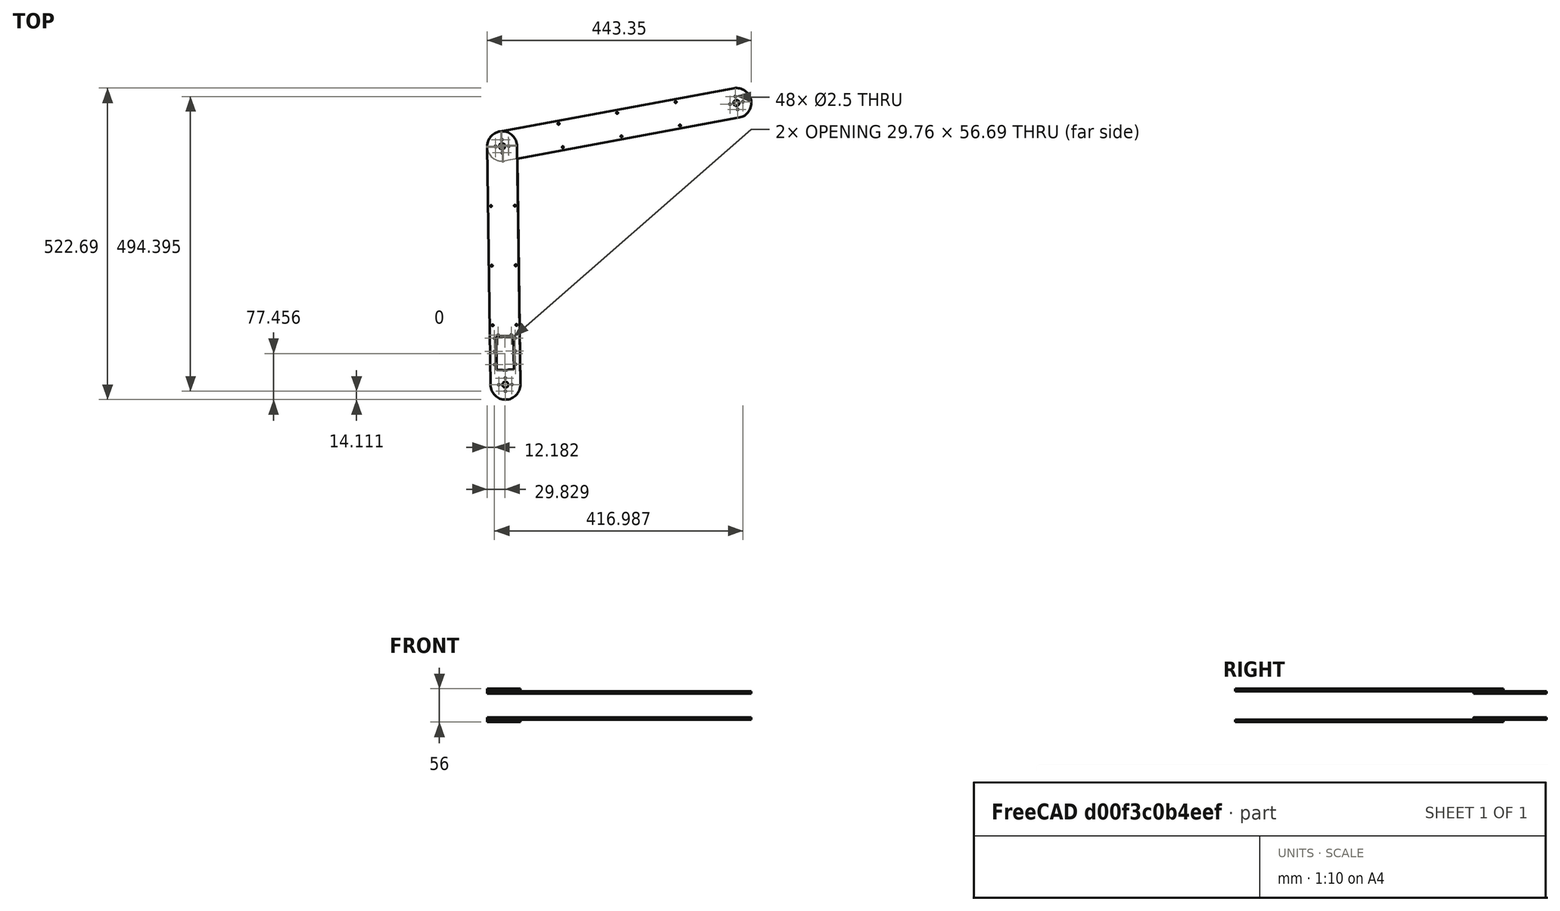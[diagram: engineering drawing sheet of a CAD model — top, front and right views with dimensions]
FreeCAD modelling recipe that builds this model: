
FCSTD DOCUMENT  (FreeCAD 1.0R39109 (Git))
Label: arm_assembly_def
License: All rights reserved
LicenseURL: https://en.wikipedia.org/wiki/All_rights_reserved
objects: App::FeaturePython×16, App::Link×10, Sketcher::SketchObject×4, PartDesign::Pad×4, PartDesign::Body×4, Assembly::JointGroup×1, Assembly::AssemblyObject×1
note: 24 computed .brp shape members not serialized (recipe doc carries the construction recipe); baked Part::Feature solids carry a one-line shape summary decoded from their .brp
EXTERNAL_REF file=srv.FCStd obj=Part__Feature
EXTERNAL_REF file=pulleys/gt2_24T_pulley_open.FCStd obj=Body
EXTERNAL_REF file=pulleys/gt2_48T_pulley.FCStd obj=Body
EXTERNAL_REF file=pulleys/gt2_48T_pulley_double.FCStd obj=Body
EXTERNAL_REF file=pulleys/gt2_24T_pulley_open.FCStd obj=Body001

FEATURE [Sketcher::SketchObject] Sketch
  ArcFitTolerance = 1e-06
  AttachmentSupport = -> [XY_Plane]
  FullyConstrained = false
  MakeInternals = false
  MapMode = 5
  sketch-geometry (67):
    g0: LineSegment [constr] StartX=1.5008e-12 StartY=20 StartZ=0 EndX=1.5008e-12 EndY=-20 EndZ=0
    g1: LineSegment [constr] StartX=-2.359e-12 StartY=0 StartZ=0 EndX=-2.359e-12 EndY=400 EndZ=0
    g2: LineSegment [constr] StartX=1.5008e-12 StartY=20 StartZ=0 EndX=1.5008e-12 EndY=25 EndZ=0
    g3: Circle CenterX=-2.359e-12 CenterY=400 CenterZ=0 NormalX=0 NormalY=0 NormalZ=1 AngleXU=0 Radius=5
    g4: Circle CenterX=-2.359e-12 CenterY=400 CenterZ=0 NormalX=0 NormalY=0 NormalZ=1 AngleXU=0 Radius=2
    g5: Circle CenterX=-10.9997 CenterY=400 CenterZ=0 NormalX=0 NormalY=0 NormalZ=1 AngleXU=0 Radius=1.25
    g6: Circle CenterX=0 CenterY=389 CenterZ=0 NormalX=0 NormalY=0 NormalZ=1 AngleXU=0 Radius=1.25
    g7: Circle CenterX=10.9997 CenterY=400 CenterZ=0 NormalX=0 NormalY=0 NormalZ=1 AngleXU=0 Radius=1.25
    g8: Circle CenterX=0 CenterY=411 CenterZ=0 NormalX=0 NormalY=0 NormalZ=1 AngleXU=0 Radius=1.25
    g9: LineSegment [constr] StartX=0 StartY=-5 StartZ=0 EndX=0 EndY=5.99996 EndZ=0
    g10: Circle [constr] CenterX=0 CenterY=0 CenterZ=0 NormalX=0 NormalY=0 NormalZ=1 AngleXU=0 Radius=14
    g11: LineSegment [constr] StartX=0 StartY=0 StartZ=0 EndX=25.23 EndY=0 EndZ=0
    g12: Circle [constr] CenterX=0 CenterY=-3.8e-05 CenterZ=0 NormalX=0 NormalY=0 NormalZ=1 AngleXU=0 Radius=11
    g13: Circle CenterX=0 CenterY=0 CenterZ=0 NormalX=0 NormalY=0 NormalZ=1 AngleXU=0 Radius=5
    g14: Circle CenterX=10.9997 CenterY=0 CenterZ=0 NormalX=0 NormalY=0 NormalZ=1 AngleXU=0 Radius=1.25
    g15: Circle CenterX=-10.9997 CenterY=0 CenterZ=0 NormalX=0 NormalY=0 NormalZ=1 AngleXU=0 Radius=1.25
    g16: Circle CenterX=0 CenterY=-10.9997 CenterZ=0 NormalX=0 NormalY=0 NormalZ=1 AngleXU=0 Radius=1.25
    g17: Circle CenterX=0 CenterY=11 CenterZ=0 NormalX=0 NormalY=0 NormalZ=1 AngleXU=0 Radius=1.25
    g18: LineSegment [constr] StartX=0 StartY=0 StartZ=0 EndX=-25 EndY=0 EndZ=0
    g19: LineSegment [constr] StartX=20.1368 StartY=86.0999 StartZ=0 EndX=20.1368 EndY=24.9999 EndZ=0
    g20: LineSegment [constr] StartX=0.036848 StartY=80.5 StartZ=0 EndX=14.5368 EndY=80.5 EndZ=0
    g21: LineSegment StartX=14.5368 StartY=80.5 StartZ=0 EndX=-14.4632 EndY=80.5 EndZ=0
    g22: LineSegment StartX=14.5368 StartY=80.5 StartZ=0 EndX=14.5368 EndY=24.9999 EndZ=0
    g23: Circle CenterX=11.0368 CenterY=83.3 CenterZ=0 NormalX=0 NormalY=0 NormalZ=1 AngleXU=0 Radius=1.25
    g24: Circle CenterX=17.3368 CenterY=78 CenterZ=0 NormalX=0 NormalY=0 NormalZ=1 AngleXU=0 Radius=1.25
    g25: LineSegment [constr] StartX=-20.0632 StartY=86.0999 StartZ=0 EndX=20.1368 EndY=86.0999 EndZ=0
    g26: Circle CenterX=17.3368 CenterY=56 CenterZ=0 NormalX=0 NormalY=0 NormalZ=1 AngleXU=0 Radius=1.25
    g27: Circle CenterX=17.3368 CenterY=34 CenterZ=0 NormalX=0 NormalY=0 NormalZ=1 AngleXU=0 Radius=1.25
    g28: Circle [constr] CenterX=0.036848 CenterY=37.9999 CenterZ=0 NormalX=0 NormalY=0 NormalZ=1 AngleXU=0 Radius=14
    g29: ArcOfCircle CenterX=0.036848 CenterY=37.9999 CenterZ=0 NormalX=0 NormalY=0 NormalZ=1 AngleXU=0 Radius=14 StartAngle=4.33214 EndAngle=5.09264
    g30: LineSegment StartX=5.233 StartY=24.9999 StartZ=0 EndX=14.5368 EndY=24.9999 EndZ=0
    g31: LineSegment [constr] StartX=14.5368 StartY=24.9999 StartZ=0 EndX=20.1368 EndY=24.9999 EndZ=0
    g32: LineSegment [constr] StartX=17.3368 StartY=56 StartZ=0 EndX=-17.2632 EndY=56 EndZ=0
    g33: LineSegment [constr] StartX=-20.0632 StartY=24.9999 StartZ=0 EndX=-20.0632 EndY=86.0999 EndZ=0
    g34: LineSegment StartX=-14.4632 StartY=80.5 StartZ=0 EndX=-14.4632 EndY=24.9999 EndZ=0
    g35: Circle CenterX=-17.2632 CenterY=78 CenterZ=0 NormalX=0 NormalY=0 NormalZ=1 AngleXU=0 Radius=1.25
    g36: Circle CenterX=-10.9632 CenterY=83.3 CenterZ=0 NormalX=0 NormalY=0 NormalZ=1 AngleXU=0 Radius=1.25
    g37: Circle CenterX=-17.2632 CenterY=56 CenterZ=0 NormalX=0 NormalY=0 NormalZ=1 AngleXU=0 Radius=1.25
    g38: Circle CenterX=-17.2632 CenterY=34 CenterZ=0 NormalX=0 NormalY=0 NormalZ=1 AngleXU=0 Radius=1.25
    g39: LineSegment StartX=-14.4632 StartY=24.9999 StartZ=0 EndX=-5.15931 EndY=24.9999 EndZ=0
    g40: LineSegment [constr] StartX=-20.0632 StartY=24.9999 StartZ=0 EndX=-14.4632 EndY=24.9999 EndZ=0
    g41: ArcOfCircle CenterX=0.115002 CenterY=3.75548e-06 CenterZ=0 NormalX=0 NormalY=0 NormalZ=1 AngleXU=0 Radius=25.115 StartAngle=3.14159 EndAngle=6.28319
    g42: ArcOfCircle CenterX=0.115002 CenterY=399.959 CenterZ=0 NormalX=0 NormalY=0 NormalZ=1 AngleXU=0 Radius=25.115 StartAngle=0 EndAngle=3.14159
    g43: LineSegment StartX=-25 StartY=3.75548e-06 StartZ=0 EndX=-25 EndY=399.959 EndZ=0
    g44: LineSegment StartX=25.23 StartY=3.75548e-06 StartZ=0 EndX=25.23 EndY=399.959 EndZ=0
    g45: LineSegment [constr] StartX=25.23 StartY=199.98 StartZ=0 EndX=-25 EndY=199.98 EndZ=0
    g46: LineSegment [constr] StartX=25.23 StartY=199.98 StartZ=0 EndX=55.23 EndY=199.98 EndZ=0
    g47: LineSegment [constr] StartX=25.23 StartY=0 StartZ=0 EndX=55.23 EndY=0 EndZ=0
    g48: LineSegment [constr] StartX=55.23 StartY=0 StartZ=0 EndX=55.23 EndY=199.98 EndZ=0
    g49: LineSegment [constr] StartX=55.23 StartY=99.9898 StartZ=0 EndX=25.23 EndY=99.9898 EndZ=0
    g50: LineSegment [constr] StartX=25.23 StartY=99.9898 StartZ=0 EndX=-25 EndY=99.9898 EndZ=0
    g51: LineSegment [constr] StartX=25.23 StartY=399.959 StartZ=0 EndX=55.23 EndY=399.959 EndZ=0
    g52: LineSegment [constr] StartX=55.23 StartY=399.959 StartZ=0 EndX=55.23 EndY=199.98 EndZ=0
    g53: LineSegment [constr] StartX=55.23 StartY=299.969 StartZ=0 EndX=25.23 EndY=299.969 EndZ=0
    g54: LineSegment [constr] StartX=25.23 StartY=299.969 StartZ=0 EndX=-25 EndY=299.969 EndZ=0
    g55: LineSegment [constr] StartX=-25 StartY=299.969 StartZ=0 EndX=-20 EndY=299.969 EndZ=0
    g56: LineSegment [constr] StartX=-20 StartY=299.969 StartZ=0 EndX=-20 EndY=199.98 EndZ=0
    g57: LineSegment [constr] StartX=-20 StartY=199.98 StartZ=0 EndX=-20 EndY=99.9898 EndZ=0
    g58: LineSegment [constr] StartX=25.23 StartY=299.969 StartZ=0 EndX=20.23 EndY=299.969 EndZ=0
    g59: LineSegment [constr] StartX=20.23 StartY=299.969 StartZ=0 EndX=20.23 EndY=199.98 EndZ=0
    g60: LineSegment [constr] StartX=20.23 StartY=199.98 StartZ=0 EndX=20.23 EndY=99.9898 EndZ=0
    g61: Circle CenterX=-20 CenterY=299.969 CenterZ=0 NormalX=0 NormalY=0 NormalZ=1 AngleXU=0 Radius=1.5
    g62: Circle CenterX=20.23 CenterY=299.969 CenterZ=0 NormalX=0 NormalY=0 NormalZ=1 AngleXU=0 Radius=1.5
    g63: Circle CenterX=-20 CenterY=199.98 CenterZ=0 NormalX=0 NormalY=0 NormalZ=1 AngleXU=0 Radius=1.5
    g64: Circle CenterX=20.23 CenterY=199.98 CenterZ=0 NormalX=0 NormalY=0 NormalZ=1 AngleXU=0 Radius=1.5
    g65: Circle CenterX=-20 CenterY=99.9898 CenterZ=0 NormalX=0 NormalY=0 NormalZ=1 AngleXU=0 Radius=1.5
    g66: Circle CenterX=20.23 CenterY=99.9898 CenterZ=0 NormalX=0 NormalY=0 NormalZ=1 AngleXU=0 Radius=1.5
  constraints (132):
    c: Vertical(g0)
    c: Vertical(g1)
    c: Coincident(g2,g0)
    c: Vertical(g2)
    c: Diameter(g3) = 10
    c: Coincident(g3,g1)
    c: Diameter(g4) = 4
    c: Coincident(g4,g1)
    c: Diameter(g8) = 2.5
    c: Diameter(g5) = 2.5
    c: Diameter(g6) = 2.5
    c: Diameter(g7) = 2.5
    c: Vertical(g9)
    c: Diameter(g10) = 28
    c: Coincident(g18,g10)
    c: Horizontal(g18)
    c: Coincident(g11,g10)
    c: Horizontal(g11)
    c: Diameter(g12) = 22
    c: Diameter(g13) = 10
    c: Coincident(g13,g10)
    c: Diameter(g17) = 2.5
    c: Diameter(g15) = 2.5
    c: Diameter(g16) = 2.5
    c: Diameter(g14) = 2.5
    c: Coincident(g25,g19)
    c: Coincident(g33,g25)
    c: Horizontal(g25)
    c: Vertical(g19)
    c: Vertical(g33)
    c: Distance(g19,g33) = 40.2
    c: Distance(g25,g33) = 61.1
    c: Diameter(g29) = 28
    c: Horizontal(g20)
    c: Coincident(g21,g20)
    c: Horizontal(g21)
    c: Coincident(g34,g21)
    c: Vertical(g34)
    c: Coincident(g22,g20)
    c: Vertical(g22)
    c: Diameter(g23) = 2.5
    c: Equal(g23,g36)
    c: Equal(g23,g27)
    c: Equal(g23,g38)
    c: Equal(g23,g37)
    c: Equal(g23,g35)
    c: Equal(g23,g24)
    c: Equal(g23,g26)
    c: Coincident(g28,g29)
    c: PointOnObject(g29,g28)
    c: Coincident(g30,g29)
    c: Coincident(g30,g22)
    c: Horizontal(g30)
    c: Coincident(g31,g22)
    c: Coincident(g31,g19)
    c: Horizontal(g31)
    c: Coincident(g39,g34)
    c: Coincident(g39,g29)
    c: Horizontal(g39)
    c: Coincident(g40,g33)
    c: Coincident(g40,g34)
    c: Horizontal(g40)
    c: Coincident(g32,g26)
    c: Coincident(g32,g37)
    c: Horizontal(g32)
    c: DistanceY(g28,g1) = 362
    c: Tangent(g41,g43) = 1.5708
    c: Tangent(g41,g44) = -1.5708
    c: Tangent(g42,g43) = 1.5708
    c: Tangent(g42,g44) = -1.5708
    c: Equal(g41,g42)
    c: Symmetric(g44,g44,g45)
    c: Symmetric(g43,g43,g45)
    c: Horizontal(g45)
    c: Distance(g46) = 30
    c: Horizontal(g46)
    c: Coincident(g46,g45)
    c: Distance(g47) = 30
    c: Horizontal(g47)
    c: Coincident(g47,g11)
    c: PointOnObject(g47,g-1)
    c: Coincident(g48,g47)
    c: Coincident(g48,g46)
    c: Vertical(g48)
    c: Symmetric(g48,g48,g49)
    c: PointOnObject(g49,g44)
    c: Horizontal(g49)
    c: Coincident(g50,g49)
    c: PointOnObject(g50,g43)
    c: Horizontal(g50)
    c: Distance(g51) = 30
    c: Horizontal(g51)
    c: Coincident(g51,g42)
    c: Coincident(g52,g51)
    c: Coincident(g52,g46)
    c: Symmetric(g52,g52,g53)
    c: PointOnObject(g53,g44)
    c: Horizontal(g53)
    c: Coincident(g54,g53)
    c: PointOnObject(g54,g43)
    c: Horizontal(g54)
    c: Distance(g55) = 5
    c: Coincident(g55,g54)
    c: PointOnObject(g55,g54)
    c: Coincident(g56,g55)
    c: PointOnObject(g56,g45)
    c: Vertical(g56)
    c: Coincident(g57,g56)
    c: PointOnObject(g57,g50)
    c: Vertical(g57)
    c: Distance(g58) = 5
    c: Coincident(g58,g53)
    c: PointOnObject(g58,g54)
    c: Coincident(g59,g58)
    c: PointOnObject(g59,g45)
    c: Vertical(g59)
    c: Coincident(g60,g59)
    c: PointOnObject(g60,g50)
    c: Vertical(g60)
    c: Coincident(g61,g55)
    c: Diameter(g61) = 3
    c: Coincident(g62,g58)
    c: Equal(g61,g62)
    c: Coincident(g63,g56)
    c: Equal(g61,g63)
    c: Coincident(g64,g59)
    c: Equal(g63,g64)
    c: Coincident(g65,g57)
    c: Equal(g63,g65)
    c: Coincident(g66,g60)
    c: Equal(g65,g66)
    c: DistanceY(g41,g28) = 37.9999
FEATURE [Sketcher::SketchObject] Sketch001
  ArcFitTolerance = 1e-06
  FullyConstrained = false
  MakeInternals = false
  MapMode = 5
  sketch-geometry (41):
    g0: Circle [constr] CenterX=7e-16 CenterY=0.000303 CenterZ=0 NormalX=0 NormalY=0 NormalZ=1 AngleXU=0 Radius=14
    g1: LineSegment [constr] StartX=7e-16 StartY=0.000303 StartZ=0 EndX=7e-16 EndY=400.001 EndZ=0
    g2: Circle CenterX=7e-16 CenterY=400.001 CenterZ=0 NormalX=0 NormalY=0 NormalZ=1 AngleXU=0 Radius=5
    g3: Circle CenterX=7e-16 CenterY=0 CenterZ=0 NormalX=0 NormalY=0 NormalZ=1 AngleXU=0 Radius=5
    g4: Circle CenterX=7e-16 CenterY=400.001 CenterZ=0 NormalX=0 NormalY=0 NormalZ=1 AngleXU=0 Radius=2
    g5: Circle CenterX=7e-16 CenterY=0.000303 CenterZ=0 NormalX=0 NormalY=0 NormalZ=1 AngleXU=0 Radius=2
    g6: Circle [constr] CenterX=0 CenterY=0 CenterZ=0 NormalX=0 NormalY=0 NormalZ=1 AngleXU=0 Radius=11
    g7: ArcOfCircle CenterX=7e-16 CenterY=0 CenterZ=0 NormalX=0 NormalY=0 NormalZ=1 AngleXU=0 Radius=25 StartAngle=3.14159 EndAngle=6.28319
    g8: ArcOfCircle CenterX=7e-16 CenterY=400.001 CenterZ=0 NormalX=0 NormalY=0 NormalZ=1 AngleXU=0 Radius=25 StartAngle=6e-16 EndAngle=3.14159
    g9: LineSegment StartX=-25 StartY=-8e-15 StartZ=0 EndX=-25 EndY=400.001 EndZ=0
    g10: LineSegment StartX=25 StartY=0 StartZ=0 EndX=25 EndY=400.001 EndZ=0
    g11: Circle CenterX=10.9997 CenterY=400.001 CenterZ=0 NormalX=0 NormalY=0 NormalZ=1 AngleXU=0 Radius=1.25
    g12: Circle CenterX=0 CenterY=411.001 CenterZ=0 NormalX=0 NormalY=0 NormalZ=1 AngleXU=0 Radius=1.25
    g13: Circle CenterX=-10.9997 CenterY=400.001 CenterZ=0 NormalX=0 NormalY=0 NormalZ=1 AngleXU=0 Radius=1.25
    g14: Circle CenterX=0 CenterY=389.001 CenterZ=0 NormalX=0 NormalY=0 NormalZ=1 AngleXU=0 Radius=1.25
    g15: Circle CenterX=10.9997 CenterY=0.000303 CenterZ=0 NormalX=0 NormalY=0 NormalZ=1 AngleXU=0 Radius=1.25
    g16: Circle CenterX=0 CenterY=11 CenterZ=0 NormalX=0 NormalY=0 NormalZ=1 AngleXU=0 Radius=1.25
    g17: Circle CenterX=-10.9997 CenterY=0.000303 CenterZ=0 NormalX=0 NormalY=0 NormalZ=1 AngleXU=0 Radius=1.25
    g18: Circle CenterX=0 CenterY=-10.9994 CenterZ=0 NormalX=0 NormalY=0 NormalZ=1 AngleXU=0 Radius=1.25
    g19: LineSegment [constr] StartX=25 StartY=200 StartZ=0 EndX=-25 EndY=200 EndZ=0
    g20: LineSegment [constr] StartX=25 StartY=200 StartZ=0 EndX=55 EndY=200 EndZ=0
    g21: LineSegment [constr] StartX=25 StartY=0 StartZ=0 EndX=55 EndY=0 EndZ=0
    g22: LineSegment [constr] StartX=25 StartY=400.001 StartZ=0 EndX=55 EndY=400.001 EndZ=0
    g23: LineSegment [constr] StartX=55 StartY=200 StartZ=0 EndX=55 EndY=400.001 EndZ=0
    g24: LineSegment [constr] StartX=55 StartY=200 StartZ=0 EndX=55 EndY=0 EndZ=0
    g25: LineSegment [constr] StartX=55 StartY=100 StartZ=0 EndX=25 EndY=100 EndZ=0
    g26: LineSegment [constr] StartX=25 StartY=100 StartZ=0 EndX=-25 EndY=100 EndZ=0
    g27: LineSegment [constr] StartX=55 StartY=300 StartZ=0 EndX=25 EndY=300 EndZ=0
    g28: LineSegment [constr] StartX=25 StartY=300 StartZ=0 EndX=-25 EndY=300 EndZ=0
    g29: LineSegment [constr] StartX=-25 StartY=300 StartZ=0 EndX=-20 EndY=300 EndZ=0
    g30: LineSegment [constr] StartX=-20 StartY=300 StartZ=0 EndX=-20 EndY=200 EndZ=0
    g31: LineSegment [constr] StartX=-20 StartY=200 StartZ=0 EndX=-20 EndY=100 EndZ=0
    g32: LineSegment [constr] StartX=25 StartY=100 StartZ=0 EndX=20 EndY=100 EndZ=0
    g33: LineSegment [constr] StartX=20 StartY=100 StartZ=0 EndX=20 EndY=200 EndZ=0
    g34: LineSegment [constr] StartX=20 StartY=200 StartZ=0 EndX=20 EndY=300 EndZ=0
    g35: Circle CenterX=-20 CenterY=300 CenterZ=0 NormalX=0 NormalY=0 NormalZ=1 AngleXU=0 Radius=1.5
    g36: Circle CenterX=20 CenterY=300 CenterZ=0 NormalX=0 NormalY=0 NormalZ=1 AngleXU=0 Radius=1.5
    g37: Circle CenterX=-20 CenterY=200 CenterZ=0 NormalX=0 NormalY=0 NormalZ=1 AngleXU=0 Radius=1.5
    g38: Circle CenterX=20 CenterY=200 CenterZ=0 NormalX=0 NormalY=0 NormalZ=1 AngleXU=0 Radius=1.5
    g39: Circle CenterX=-20 CenterY=100 CenterZ=0 NormalX=0 NormalY=0 NormalZ=1 AngleXU=0 Radius=1.5
    g40: Circle CenterX=20 CenterY=100 CenterZ=0 NormalX=0 NormalY=0 NormalZ=1 AngleXU=0 Radius=1.5
  constraints (85):
    c: Diameter(g0) = 28
    c: Coincident(g1,g0)
    c: Vertical(g1)
    c: Coincident(g2,g1)
    c: Diameter(g3) = 10
    c: Diameter(g4) = 4
    c: Coincident(g4,g1)
    c: Diameter(g5) = 4
    c: Coincident(g5,g0)
    c: Diameter(g6) = 22
    c: Tangent(g7,g9) = 1.5708
    c: Tangent(g7,g10) = -1.5708
    c: Tangent(g8,g9) = 1.5708
    c: Tangent(g8,g10) = -1.5708
    c: Equal(g7,g8)
    c: Radius(g7) = 25
    c: Coincident(g7,g3)
    c: Coincident(g8,g1)
    c: Vertical(g9)
    c: Diameter(g12) = 2.5
    c: Diameter(g13) = 2.5
    c: Diameter(g14) = 2.5
    c: Diameter(g11) = 2.5
    c: Diameter(g16) = 2.5
    c: Diameter(g17) = 2.5
    c: Diameter(g18) = 2.5
    c: Diameter(g15) = 2.5
    c: Symmetric(g10,g10,g19)
    c: Symmetric(g9,g9,g19)
    c: Distance(g20) = 30
    c: Horizontal(g20)
    c: Coincident(g20,g19)
    c: Distance(g21) = 30
    c: Horizontal(g21)
    c: Coincident(g21,g7)
    c: PointOnObject(g21,g-1)
    c: Distance(g22) = 30
    c: Horizontal(g22)
    c: Coincident(g22,g8)
    c: Coincident(g23,g20)
    c: Coincident(g23,g22)
    c: Coincident(g24,g20)
    c: Coincident(g24,g21)
    c: Symmetric(g24,g24,g25)
    c: PointOnObject(g25,g10)
    c: Horizontal(g25)
    c: Coincident(g26,g25)
    c: PointOnObject(g26,g9)
    c: Horizontal(g26)
    c: Symmetric(g23,g23,g27)
    c: PointOnObject(g27,g10)
    c: Horizontal(g27)
    c: Coincident(g28,g27)
    c: PointOnObject(g28,g9)
    c: Horizontal(g28)
    c: Distance(g29) = 5
    c: Horizontal(g29)
    c: Coincident(g29,g28)
    c: Coincident(g30,g29)
    c: PointOnObject(g30,g19)
    c: Vertical(g30)
    c: Coincident(g31,g30)
    c: PointOnObject(g31,g26)
    c: Vertical(g31)
    c: Distance(g32) = 5
    c: Horizontal(g32)
    c: Coincident(g32,g25)
    c: Coincident(g33,g32)
    c: PointOnObject(g33,g19)
    c: Vertical(g33)
    c: Coincident(g34,g33)
    c: PointOnObject(g34,g28)
    c: Vertical(g34)
    c: Diameter(g35) = 3
    c: Coincident(g35,g29)
    c: Coincident(g36,g34)
    c: Equal(g35,g36)
    c: Coincident(g37,g30)
    c: Equal(g35,g37)
    c: Coincident(g38,g33)
    c: Equal(g37,g38)
    c: Coincident(g39,g31)
    c: Equal(g37,g39)
    c: Coincident(g40,g32)
    c: Equal(g39,g40)
FEATURE [PartDesign::Pad] Pad
  Direction = (0,0,1)
  Length = 4
  Length2 = 10
  Profile = -> Sketch
  ReferenceAxis = -> Sketch [N_Axis]
  Refine = true
  Suppressed = false
  Type = 0
FEATURE [PartDesign::Body] Body  label="arm_low_1"
  AllowCompound = false
  Group = -> [Sketch,Pad]
  Origin = -> Origin
  Placement = pos=(0,0,25.3) rot=(0,0,1;0.013804rad)
  Tip = -> Pad
FEATURE [PartDesign::Pad] Pad001
  Direction = (0,0,1)
  Length = 4
  Length2 = 10
  Profile = -> Sketch001
  ReferenceAxis = -> Sketch001 [N_Axis]
  Refine = true
  Suppressed = false
  Type = 0
FEATURE [PartDesign::Body] Body001  label="arm_high_1"
  AllowCompound = false
  Group = -> [Sketch001,Pad001]
  Origin = -> Origin001
  Placement = pos=(387.832,472.58,29.3) rot=(0,0,1;1.75335rad)
  Tip = -> Pad001
FEATURE [App::Link] DC05_M01_DUMMY
  LinkedObject = -> <external srv.FCStd>#Part__Feature
FEATURE [App::FeaturePython] GroundedJoint  # Assembly grounded joint (typed FeaturePython)
  ObjectToGround = -> DC05_M01_DUMMY
FEATURE [App::FeaturePython] Joint  label="Revolute"  # Assembly joint (typed FeaturePython)
  Activated = true
  AngleMax = 0
  AngleMin = 0
  Detach1 = false
  Detach2 = false
  Distance = 0
  Distance2 = 0
  EnableAngleMax = false
  EnableAngleMin = false
  EnableLengthMax = false
  EnableLengthMin = false
  JointType = 1 (Revolute)
  LengthMax = 0
  LengthMin = 0
  Placement2 = pos=(0,0,25.3) rot=(-0.707107,0.707107,0;3.14159rad)
  Reference1 = -> Assembly [Body.Face11,Body.Edge2]
  Reference2 = -> Assembly [DC05_M01_DUMMY.Face269,DC05_M01_DUMMY.Edge1]
FEATURE [App::FeaturePython] Joint001  label="Revolute001"  # Assembly joint (typed FeaturePython)
  Activated = true
  AngleMax = 0
  AngleMin = 0
  Detach1 = false
  Detach2 = false
  Distance = 0
  Distance2 = 0
  EnableAngleMax = false
  EnableAngleMin = false
  EnableLengthMax = false
  EnableLengthMin = false
  JointType = 1 (Revolute)
  LengthMax = 0
  LengthMin = 0
  Placement1 = pos=(5.68e-14,400.001,0) rot=(0,0,1;0rad)
  Placement2 = pos=(-2.3599e-12,400,4) rot=(0,0,1;0rad)
  Reference1 = -> Assembly [Body001.Edge17,Body001.Edge17]
  Reference2 = -> Assembly [Body.Edge36,Body.Edge36]
FEATURE [App::Link] DC05_M01_DUMMY001
  LinkPlacement = pos=(-0.487674,37.9968,9.05) rot=(0,0,1;3.1554rad)
  LinkedObject = -> <external srv.FCStd>#Part__Feature
  Placement = pos=(-0.487674,37.9968,9.05) rot=(0,0,1;3.1554rad)
FEATURE [App::FeaturePython] Joint002  label="Distance"  # Assembly joint (typed FeaturePython)
  Activated = true
  AngleMax = 0
  AngleMin = 0
  Detach1 = false
  Detach2 = false
  Distance = 0
  Distance2 = 0
  EnableAngleMax = false
  EnableAngleMin = false
  EnableLengthMax = false
  EnableLengthMin = false
  JointType = 5 (Distance)
  LengthMax = 0
  LengthMin = 0
  Placement1 = pos=(0.00149626,-23.2403,17) rot=(0,0,1;0rad)
  Placement2 = pos=(-10.9997,0,2) rot=(0,0,1;0rad)
  Reference1 = -> Assembly [DC05_M01_DUMMY001.Face128,DC05_M01_DUMMY001.Vertex405]
  Reference2 = -> Assembly [Body.Face29,Body.Edge23]
FEATURE [App::FeaturePython] Joint003  label="Distance001"  # Assembly joint (typed FeaturePython)
  Activated = true
  AngleMax = 0
  AngleMin = 0
  Detach1 = false
  Detach2 = false
  Distance = -55.5
  Distance2 = 0
  EnableAngleMax = false
  EnableAngleMin = false
  EnableLengthMax = false
  EnableLengthMin = false
  JointType = 5 (Distance)
  LengthMax = 0
  LengthMin = 0
  Placement1 = pos=(3.76754e-09,-42.5,18.25) rot=(1,0,0;1.5708rad)
  Placement2 = pos=(-9.81123,24.9999,2) rot=(-1,0,0;1.5708rad)
  Reference1 = -> Assembly [DC05_M01_DUMMY001.Face34,DC05_M01_DUMMY001.Face34]
  Reference2 = -> Assembly [Body.Face7,Body.Face7]
FEATURE [App::FeaturePython] Joint004  label="Distance002"  # Assembly joint (typed FeaturePython)
  Activated = true
  AngleMax = 0
  AngleMin = 0
  Detach1 = false
  Detach2 = false
  Distance = -28.5
  Distance2 = 0
  EnableAngleMax = false
  EnableAngleMin = false
  EnableLengthMax = false
  EnableLengthMin = false
  JointType = 5 (Distance)
  LengthMax = 0
  LengthMin = 0
  Placement1 = pos=(-14.5,-15.25,18.25) rot=(0.57735,-0.57735,-0.57735;2.0944rad)
  Placement2 = pos=(0.036848,37.9999,2) rot=(0,0,1;0rad)
  Reference1 = -> Assembly [DC05_M01_DUMMY001.Face46,DC05_M01_DUMMY001.Face46]
  Reference2 = -> Assembly [Body.Face8,Body.Face8]
FEATURE [App::Link] Body002  label="Body"
  LinkPlacement = pos=(-0.487674,37.9968,38.55) rot=(0,0,-1;1.55699rad)
  LinkedObject = -> <external pulleys/gt2_24T_pulley_open.FCStd>#Body
  Placement = pos=(-0.487674,37.9968,38.55) rot=(0,0,-1;1.55699rad)
FEATURE [App::FeaturePython] Joint005  label="Fixed"  # Assembly joint (typed FeaturePython)
  Activated = true
  AngleMax = 0
  AngleMin = 0
  Detach1 = false
  Detach2 = false
  Distance = 0
  Distance2 = 0
  EnableAngleMax = false
  EnableAngleMin = false
  EnableLengthMax = false
  EnableLengthMin = false
  JointType = 0 (Fixed)
  LengthMax = 0
  LengthMin = 0
  Placement1 = pos=(0,0,-6) rot=(1,0,0;3.14159rad)
  Placement2 = pos=(0,0,23.5) rot=(-0.707107,-0.707107,0;3.14159rad)
  Reference1 = -> Assembly [Body002.Edge529,Body002.Edge529]
  Reference2 = -> Assembly [DC05_M01_DUMMY001.Edge888,DC05_M01_DUMMY001.Edge888]
FEATURE [App::Link] Body003
  LinkPlacement = pos=(-5.52126,399.962,35.3) rot=(0,0,1;1.75335rad)
  LinkedObject = -> <external pulleys/gt2_48T_pulley.FCStd>#Body
  Placement = pos=(-5.52126,399.962,35.3) rot=(0,0,1;1.75335rad)
FEATURE [App::FeaturePython] Joint006  label="Fixed001"  # Assembly joint (typed FeaturePython)
  Activated = true
  AngleMax = 0
  AngleMin = 0
  Detach1 = false
  Detach2 = false
  Distance = 0
  Distance2 = 0
  EnableAngleMax = false
  EnableAngleMin = false
  EnableLengthMax = false
  EnableLengthMin = false
  JointType = 0 (Fixed)
  LengthMax = 0
  LengthMin = 0
  Placement1 = pos=(0,0,-2) rot=(1,0,0;3.14159rad)
  Placement2 = pos=(5.68e-14,400.001,4) rot=(0,0,1;0rad)
  Reference1 = -> Assembly [Body003.Edge875,Body003.Edge875]
  Reference2 = -> Assembly [Body001.Edge18,Body001.Edge18]
FEATURE [Sketcher::SketchObject] Sketch002
  ArcFitTolerance = 1e-06
  AttachmentSupport = -> [XY_Plane004]
  FullyConstrained = false
  MakeInternals = false
  MapMode = 5
  sketch-geometry (67):
    g0: LineSegment [constr] StartX=1.5008e-12 StartY=20 StartZ=0 EndX=1.5008e-12 EndY=-20 EndZ=0
    g1: LineSegment [constr] StartX=-2.359e-12 StartY=0 StartZ=0 EndX=-2.359e-12 EndY=400 EndZ=0
    g2: LineSegment [constr] StartX=1.5008e-12 StartY=20 StartZ=0 EndX=1.5008e-12 EndY=25 EndZ=0
    g3: Circle CenterX=-2.359e-12 CenterY=400 CenterZ=0 NormalX=0 NormalY=0 NormalZ=1 AngleXU=0 Radius=5
    g4: Circle CenterX=-2.359e-12 CenterY=400 CenterZ=0 NormalX=0 NormalY=0 NormalZ=1 AngleXU=0 Radius=2
    g5: Circle CenterX=-10.9997 CenterY=400 CenterZ=0 NormalX=0 NormalY=0 NormalZ=1 AngleXU=0 Radius=1.25
    g6: Circle CenterX=0 CenterY=389 CenterZ=0 NormalX=0 NormalY=0 NormalZ=1 AngleXU=0 Radius=1.25
    g7: Circle CenterX=10.9997 CenterY=400 CenterZ=0 NormalX=0 NormalY=0 NormalZ=1 AngleXU=0 Radius=1.25
    g8: Circle CenterX=0 CenterY=411 CenterZ=0 NormalX=0 NormalY=0 NormalZ=1 AngleXU=0 Radius=1.25
    g9: LineSegment [constr] StartX=0 StartY=-5 StartZ=0 EndX=0 EndY=5.99996 EndZ=0
    g10: Circle [constr] CenterX=0 CenterY=0 CenterZ=0 NormalX=0 NormalY=0 NormalZ=1 AngleXU=0 Radius=14
    g11: LineSegment [constr] StartX=0 StartY=0 StartZ=0 EndX=25.23 EndY=0 EndZ=0
    g12: Circle [constr] CenterX=0 CenterY=-3.8e-05 CenterZ=0 NormalX=0 NormalY=0 NormalZ=1 AngleXU=0 Radius=11
    g13: Circle CenterX=0 CenterY=0 CenterZ=0 NormalX=0 NormalY=0 NormalZ=1 AngleXU=0 Radius=5
    g14: Circle CenterX=10.9997 CenterY=0 CenterZ=0 NormalX=0 NormalY=0 NormalZ=1 AngleXU=0 Radius=1.25
    g15: Circle CenterX=-10.9997 CenterY=0 CenterZ=0 NormalX=0 NormalY=0 NormalZ=1 AngleXU=0 Radius=1.25
    g16: Circle CenterX=0 CenterY=-10.9997 CenterZ=0 NormalX=0 NormalY=0 NormalZ=1 AngleXU=0 Radius=1.25
    g17: Circle CenterX=0 CenterY=11 CenterZ=0 NormalX=0 NormalY=0 NormalZ=1 AngleXU=0 Radius=1.25
    g18: LineSegment [constr] StartX=0 StartY=0 StartZ=0 EndX=-25 EndY=0 EndZ=0
    g19: LineSegment [constr] StartX=20.1368 StartY=86.0999 StartZ=0 EndX=20.1368 EndY=24.9999 EndZ=0
    g20: LineSegment [constr] StartX=0.036848 StartY=80.5 StartZ=0 EndX=14.5368 EndY=80.5 EndZ=0
    g21: LineSegment StartX=14.5368 StartY=80.5 StartZ=0 EndX=-14.4632 EndY=80.5 EndZ=0
    g22: LineSegment StartX=14.5368 StartY=80.5 StartZ=0 EndX=14.5368 EndY=24.9999 EndZ=0
    g23: Circle CenterX=11.0368 CenterY=83.3 CenterZ=0 NormalX=0 NormalY=0 NormalZ=1 AngleXU=0 Radius=1.25
    g24: Circle CenterX=17.3368 CenterY=78 CenterZ=0 NormalX=0 NormalY=0 NormalZ=1 AngleXU=0 Radius=1.25
    g25: LineSegment [constr] StartX=-20.0632 StartY=86.0999 StartZ=0 EndX=20.1368 EndY=86.0999 EndZ=0
    g26: Circle CenterX=17.3368 CenterY=56 CenterZ=0 NormalX=0 NormalY=0 NormalZ=1 AngleXU=0 Radius=1.25
    g27: Circle CenterX=17.3368 CenterY=34 CenterZ=0 NormalX=0 NormalY=0 NormalZ=1 AngleXU=0 Radius=1.25
    g28: Circle [constr] CenterX=0.036848 CenterY=37.9999 CenterZ=0 NormalX=0 NormalY=0 NormalZ=1 AngleXU=0 Radius=14
    g29: ArcOfCircle CenterX=0.036848 CenterY=37.9999 CenterZ=0 NormalX=0 NormalY=0 NormalZ=1 AngleXU=0 Radius=14 StartAngle=4.33214 EndAngle=5.09264
    g30: LineSegment StartX=5.233 StartY=24.9999 StartZ=0 EndX=14.5368 EndY=24.9999 EndZ=0
    g31: LineSegment [constr] StartX=14.5368 StartY=24.9999 StartZ=0 EndX=20.1368 EndY=24.9999 EndZ=0
    g32: LineSegment [constr] StartX=17.3368 StartY=56 StartZ=0 EndX=-17.2632 EndY=56 EndZ=0
    g33: LineSegment [constr] StartX=-20.0632 StartY=24.9999 StartZ=0 EndX=-20.0632 EndY=86.0999 EndZ=0
    g34: LineSegment StartX=-14.4632 StartY=80.5 StartZ=0 EndX=-14.4632 EndY=24.9999 EndZ=0
    g35: Circle CenterX=-17.2632 CenterY=78 CenterZ=0 NormalX=0 NormalY=0 NormalZ=1 AngleXU=0 Radius=1.25
    g36: Circle CenterX=-10.9632 CenterY=83.3 CenterZ=0 NormalX=0 NormalY=0 NormalZ=1 AngleXU=0 Radius=1.25
    g37: Circle CenterX=-17.2632 CenterY=56 CenterZ=0 NormalX=0 NormalY=0 NormalZ=1 AngleXU=0 Radius=1.25
    g38: Circle CenterX=-17.2632 CenterY=34 CenterZ=0 NormalX=0 NormalY=0 NormalZ=1 AngleXU=0 Radius=1.25
    g39: LineSegment StartX=-14.4632 StartY=24.9999 StartZ=0 EndX=-5.15931 EndY=24.9999 EndZ=0
    g40: LineSegment [constr] StartX=-20.0632 StartY=24.9999 StartZ=0 EndX=-14.4632 EndY=24.9999 EndZ=0
    g41: ArcOfCircle CenterX=0.115002 CenterY=3.75548e-06 CenterZ=0 NormalX=0 NormalY=0 NormalZ=1 AngleXU=0 Radius=25.115 StartAngle=3.14159 EndAngle=6.28319
    g42: ArcOfCircle CenterX=0.115002 CenterY=399.959 CenterZ=0 NormalX=0 NormalY=0 NormalZ=1 AngleXU=0 Radius=25.115 StartAngle=0 EndAngle=3.14159
    g43: LineSegment StartX=-25 StartY=3.75548e-06 StartZ=0 EndX=-25 EndY=399.959 EndZ=0
    g44: LineSegment StartX=25.23 StartY=3.75548e-06 StartZ=0 EndX=25.23 EndY=399.959 EndZ=0
    g45: LineSegment [constr] StartX=25.23 StartY=199.98 StartZ=0 EndX=-25 EndY=199.98 EndZ=0
    g46: LineSegment [constr] StartX=25.23 StartY=199.98 StartZ=0 EndX=55.23 EndY=199.98 EndZ=0
    g47: LineSegment [constr] StartX=25.23 StartY=0 StartZ=0 EndX=55.23 EndY=0 EndZ=0
    g48: LineSegment [constr] StartX=55.23 StartY=0 StartZ=0 EndX=55.23 EndY=199.98 EndZ=0
    g49: LineSegment [constr] StartX=55.23 StartY=99.9898 StartZ=0 EndX=25.23 EndY=99.9898 EndZ=0
    g50: LineSegment [constr] StartX=25.23 StartY=99.9898 StartZ=0 EndX=-25 EndY=99.9898 EndZ=0
    g51: LineSegment [constr] StartX=25.23 StartY=399.959 StartZ=0 EndX=55.23 EndY=399.959 EndZ=0
    g52: LineSegment [constr] StartX=55.23 StartY=399.959 StartZ=0 EndX=55.23 EndY=199.98 EndZ=0
    g53: LineSegment [constr] StartX=55.23 StartY=299.969 StartZ=0 EndX=25.23 EndY=299.969 EndZ=0
    g54: LineSegment [constr] StartX=25.23 StartY=299.969 StartZ=0 EndX=-25 EndY=299.969 EndZ=0
    g55: LineSegment [constr] StartX=-25 StartY=299.969 StartZ=0 EndX=-20 EndY=299.969 EndZ=0
    g56: LineSegment [constr] StartX=-20 StartY=299.969 StartZ=0 EndX=-20 EndY=199.98 EndZ=0
    g57: LineSegment [constr] StartX=-20 StartY=199.98 StartZ=0 EndX=-20 EndY=99.9898 EndZ=0
    g58: LineSegment [constr] StartX=25.23 StartY=299.969 StartZ=0 EndX=20.23 EndY=299.969 EndZ=0
    g59: LineSegment [constr] StartX=20.23 StartY=299.969 StartZ=0 EndX=20.23 EndY=199.98 EndZ=0
    g60: LineSegment [constr] StartX=20.23 StartY=199.98 StartZ=0 EndX=20.23 EndY=99.9898 EndZ=0
    g61: Circle CenterX=-20 CenterY=299.969 CenterZ=0 NormalX=0 NormalY=0 NormalZ=1 AngleXU=0 Radius=1.5
    g62: Circle CenterX=20.23 CenterY=299.969 CenterZ=0 NormalX=0 NormalY=0 NormalZ=1 AngleXU=0 Radius=1.5
    g63: Circle CenterX=-20 CenterY=199.98 CenterZ=0 NormalX=0 NormalY=0 NormalZ=1 AngleXU=0 Radius=1.5
    g64: Circle CenterX=20.23 CenterY=199.98 CenterZ=0 NormalX=0 NormalY=0 NormalZ=1 AngleXU=0 Radius=1.5
    g65: Circle CenterX=-20 CenterY=99.9898 CenterZ=0 NormalX=0 NormalY=0 NormalZ=1 AngleXU=0 Radius=1.5
    g66: Circle CenterX=20.23 CenterY=99.9898 CenterZ=0 NormalX=0 NormalY=0 NormalZ=1 AngleXU=0 Radius=1.5
  constraints (132):
    c: Vertical(g0)
    c: Vertical(g1)
    c: Coincident(g2,g0)
    c: Vertical(g2)
    c: Diameter(g3) = 10
    c: Coincident(g3,g1)
    c: Diameter(g4) = 4
    c: Coincident(g4,g1)
    c: Diameter(g8) = 2.5
    c: Diameter(g5) = 2.5
    c: Diameter(g6) = 2.5
    c: Diameter(g7) = 2.5
    c: Vertical(g9)
    c: Diameter(g10) = 28
    c: Coincident(g18,g10)
    c: Horizontal(g18)
    c: Coincident(g11,g10)
    c: Horizontal(g11)
    c: Diameter(g12) = 22
    c: Diameter(g13) = 10
    c: Coincident(g13,g10)
    c: Diameter(g17) = 2.5
    c: Diameter(g15) = 2.5
    c: Diameter(g16) = 2.5
    c: Diameter(g14) = 2.5
    c: Coincident(g25,g19)
    c: Coincident(g33,g25)
    c: Horizontal(g25)
    c: Vertical(g19)
    c: Vertical(g33)
    c: Distance(g19,g33) = 40.2
    c: Distance(g25,g33) = 61.1
    c: Diameter(g29) = 28
    c: Horizontal(g20)
    c: Coincident(g21,g20)
    c: Horizontal(g21)
    c: Coincident(g34,g21)
    c: Vertical(g34)
    c: Coincident(g22,g20)
    c: Vertical(g22)
    c: Diameter(g23) = 2.5
    c: Equal(g23,g36)
    c: Equal(g23,g27)
    c: Equal(g23,g38)
    c: Equal(g23,g37)
    c: Equal(g23,g35)
    c: Equal(g23,g24)
    c: Equal(g23,g26)
    c: Coincident(g28,g29)
    c: PointOnObject(g29,g28)
    c: Coincident(g30,g29)
    c: Coincident(g30,g22)
    c: Horizontal(g30)
    c: Coincident(g31,g22)
    c: Coincident(g31,g19)
    c: Horizontal(g31)
    c: Coincident(g39,g34)
    c: Coincident(g39,g29)
    c: Horizontal(g39)
    c: Coincident(g40,g33)
    c: Coincident(g40,g34)
    c: Horizontal(g40)
    c: Coincident(g32,g26)
    c: Coincident(g32,g37)
    c: Horizontal(g32)
    c: DistanceY(g28,g1) = 362
    c: Tangent(g41,g43) = 1.5708
    c: Tangent(g41,g44) = -1.5708
    c: Tangent(g42,g43) = 1.5708
    c: Tangent(g42,g44) = -1.5708
    c: Equal(g41,g42)
    c: Symmetric(g44,g44,g45)
    c: Symmetric(g43,g43,g45)
    c: Horizontal(g45)
    c: Distance(g46) = 30
    c: Horizontal(g46)
    c: Coincident(g46,g45)
    c: Distance(g47) = 30
    c: Horizontal(g47)
    c: Coincident(g47,g11)
    c: PointOnObject(g47,g-1)
    c: Coincident(g48,g47)
    c: Coincident(g48,g46)
    c: Vertical(g48)
    c: Symmetric(g48,g48,g49)
    c: PointOnObject(g49,g44)
    c: Horizontal(g49)
    c: Coincident(g50,g49)
    c: PointOnObject(g50,g43)
    c: Horizontal(g50)
    c: Distance(g51) = 30
    c: Horizontal(g51)
    c: Coincident(g51,g42)
    c: Coincident(g52,g51)
    c: Coincident(g52,g46)
    c: Symmetric(g52,g52,g53)
    c: PointOnObject(g53,g44)
    c: Horizontal(g53)
    c: Coincident(g54,g53)
    c: PointOnObject(g54,g43)
    c: Horizontal(g54)
    c: Distance(g55) = 5
    c: Coincident(g55,g54)
    c: PointOnObject(g55,g54)
    c: Coincident(g56,g55)
    c: PointOnObject(g56,g45)
    c: Vertical(g56)
    c: Coincident(g57,g56)
    c: PointOnObject(g57,g50)
    c: Vertical(g57)
    c: Distance(g58) = 5
    c: Coincident(g58,g53)
    c: PointOnObject(g58,g54)
    c: Coincident(g59,g58)
    c: PointOnObject(g59,g45)
    c: Vertical(g59)
    c: Coincident(g60,g59)
    c: PointOnObject(g60,g50)
    c: Vertical(g60)
    c: Coincident(g61,g55)
    c: Diameter(g61) = 3
    c: Coincident(g62,g58)
    c: Equal(g61,g62)
    c: Coincident(g63,g56)
    c: Equal(g61,g63)
    c: Coincident(g64,g59)
    c: Equal(g63,g64)
    c: Coincident(g65,g57)
    c: Equal(g63,g65)
    c: Coincident(g66,g60)
    c: Equal(g65,g66)
    c: DistanceY(g41,g28) = 37.9999
FEATURE [PartDesign::Pad] Pad002
  Direction = (0,0,1)
  Length = 4
  Length2 = 10
  Profile = -> Sketch002
  ReferenceAxis = -> Sketch002 [N_Axis]
  Refine = true
  Suppressed = false
  Type = 0
FEATURE [PartDesign::Body] Body004  label="arm_low_002"
  AllowCompound = false
  Group = -> [Sketch002,Pad002]
  Origin = -> Origin004
  Placement = pos=(0,0,77.3) rot=(0,0,1;0.013804rad)
  Tip = -> Pad002
FEATURE [Sketcher::SketchObject] Sketch003
  ArcFitTolerance = 1e-06
  FullyConstrained = false
  MakeInternals = false
  MapMode = 5
  sketch-geometry (41):
    g0: Circle [constr] CenterX=7e-16 CenterY=0.000303 CenterZ=0 NormalX=0 NormalY=0 NormalZ=1 AngleXU=0 Radius=14
    g1: LineSegment [constr] StartX=7e-16 StartY=0.000303 StartZ=0 EndX=7e-16 EndY=400.001 EndZ=0
    g2: Circle CenterX=7e-16 CenterY=400.001 CenterZ=0 NormalX=0 NormalY=0 NormalZ=1 AngleXU=0 Radius=5
    g3: Circle CenterX=7e-16 CenterY=0 CenterZ=0 NormalX=0 NormalY=0 NormalZ=1 AngleXU=0 Radius=5
    g4: Circle CenterX=7e-16 CenterY=400.001 CenterZ=0 NormalX=0 NormalY=0 NormalZ=1 AngleXU=0 Radius=2
    g5: Circle CenterX=7e-16 CenterY=0.000303 CenterZ=0 NormalX=0 NormalY=0 NormalZ=1 AngleXU=0 Radius=2
    g6: Circle [constr] CenterX=0 CenterY=0 CenterZ=0 NormalX=0 NormalY=0 NormalZ=1 AngleXU=0 Radius=11
    g7: ArcOfCircle CenterX=7e-16 CenterY=0 CenterZ=0 NormalX=0 NormalY=0 NormalZ=1 AngleXU=0 Radius=25 StartAngle=3.14159 EndAngle=6.28319
    g8: ArcOfCircle CenterX=7e-16 CenterY=400.001 CenterZ=0 NormalX=0 NormalY=0 NormalZ=1 AngleXU=0 Radius=25 StartAngle=6e-16 EndAngle=3.14159
    g9: LineSegment StartX=-25 StartY=-8e-15 StartZ=0 EndX=-25 EndY=400.001 EndZ=0
    g10: LineSegment StartX=25 StartY=0 StartZ=0 EndX=25 EndY=400.001 EndZ=0
    g11: Circle CenterX=10.9997 CenterY=400.001 CenterZ=0 NormalX=0 NormalY=0 NormalZ=1 AngleXU=0 Radius=1.25
    g12: Circle CenterX=0 CenterY=411.001 CenterZ=0 NormalX=0 NormalY=0 NormalZ=1 AngleXU=0 Radius=1.25
    g13: Circle CenterX=-10.9997 CenterY=400.001 CenterZ=0 NormalX=0 NormalY=0 NormalZ=1 AngleXU=0 Radius=1.25
    g14: Circle CenterX=0 CenterY=389.001 CenterZ=0 NormalX=0 NormalY=0 NormalZ=1 AngleXU=0 Radius=1.25
    g15: Circle CenterX=10.9997 CenterY=0.000303 CenterZ=0 NormalX=0 NormalY=0 NormalZ=1 AngleXU=0 Radius=1.25
    g16: Circle CenterX=0 CenterY=11 CenterZ=0 NormalX=0 NormalY=0 NormalZ=1 AngleXU=0 Radius=1.25
    g17: Circle CenterX=-10.9997 CenterY=0.000303 CenterZ=0 NormalX=0 NormalY=0 NormalZ=1 AngleXU=0 Radius=1.25
    g18: Circle CenterX=0 CenterY=-10.9994 CenterZ=0 NormalX=0 NormalY=0 NormalZ=1 AngleXU=0 Radius=1.25
    g19: LineSegment [constr] StartX=25 StartY=200 StartZ=0 EndX=-25 EndY=200 EndZ=0
    g20: LineSegment [constr] StartX=25 StartY=200 StartZ=0 EndX=55 EndY=200 EndZ=0
    g21: LineSegment [constr] StartX=25 StartY=0 StartZ=0 EndX=55 EndY=0 EndZ=0
    g22: LineSegment [constr] StartX=25 StartY=400.001 StartZ=0 EndX=55 EndY=400.001 EndZ=0
    g23: LineSegment [constr] StartX=55 StartY=200 StartZ=0 EndX=55 EndY=400.001 EndZ=0
    g24: LineSegment [constr] StartX=55 StartY=200 StartZ=0 EndX=55 EndY=0 EndZ=0
    g25: LineSegment [constr] StartX=55 StartY=100 StartZ=0 EndX=25 EndY=100 EndZ=0
    g26: LineSegment [constr] StartX=25 StartY=100 StartZ=0 EndX=-25 EndY=100 EndZ=0
    g27: LineSegment [constr] StartX=55 StartY=300 StartZ=0 EndX=25 EndY=300 EndZ=0
    g28: LineSegment [constr] StartX=25 StartY=300 StartZ=0 EndX=-25 EndY=300 EndZ=0
    g29: LineSegment [constr] StartX=-25 StartY=300 StartZ=0 EndX=-20 EndY=300 EndZ=0
    g30: LineSegment [constr] StartX=-20 StartY=300 StartZ=0 EndX=-20 EndY=200 EndZ=0
    g31: LineSegment [constr] StartX=-20 StartY=200 StartZ=0 EndX=-20 EndY=100 EndZ=0
    g32: LineSegment [constr] StartX=25 StartY=100 StartZ=0 EndX=20 EndY=100 EndZ=0
    g33: LineSegment [constr] StartX=20 StartY=100 StartZ=0 EndX=20 EndY=200 EndZ=0
    g34: LineSegment [constr] StartX=20 StartY=200 StartZ=0 EndX=20 EndY=300 EndZ=0
    g35: Circle CenterX=-20 CenterY=300 CenterZ=0 NormalX=0 NormalY=0 NormalZ=1 AngleXU=0 Radius=1.5
    g36: Circle CenterX=20 CenterY=300 CenterZ=0 NormalX=0 NormalY=0 NormalZ=1 AngleXU=0 Radius=1.5
    g37: Circle CenterX=-20 CenterY=200 CenterZ=0 NormalX=0 NormalY=0 NormalZ=1 AngleXU=0 Radius=1.5
    g38: Circle CenterX=20 CenterY=200 CenterZ=0 NormalX=0 NormalY=0 NormalZ=1 AngleXU=0 Radius=1.5
    g39: Circle CenterX=-20 CenterY=100 CenterZ=0 NormalX=0 NormalY=0 NormalZ=1 AngleXU=0 Radius=1.5
    g40: Circle CenterX=20 CenterY=100 CenterZ=0 NormalX=0 NormalY=0 NormalZ=1 AngleXU=0 Radius=1.5
  constraints (85):
    c: Diameter(g0) = 28
    c: Coincident(g1,g0)
    c: Vertical(g1)
    c: Coincident(g2,g1)
    c: Diameter(g3) = 10
    c: Diameter(g4) = 4
    c: Coincident(g4,g1)
    c: Diameter(g5) = 4
    c: Coincident(g5,g0)
    c: Diameter(g6) = 22
    c: Tangent(g7,g9) = 1.5708
    c: Tangent(g7,g10) = -1.5708
    c: Tangent(g8,g9) = 1.5708
    c: Tangent(g8,g10) = -1.5708
    c: Equal(g7,g8)
    c: Radius(g7) = 25
    c: Coincident(g7,g3)
    c: Coincident(g8,g1)
    c: Vertical(g9)
    c: Diameter(g12) = 2.5
    c: Diameter(g13) = 2.5
    c: Diameter(g14) = 2.5
    c: Diameter(g11) = 2.5
    c: Diameter(g16) = 2.5
    c: Diameter(g17) = 2.5
    c: Diameter(g18) = 2.5
    c: Diameter(g15) = 2.5
    c: Symmetric(g10,g10,g19)
    c: Symmetric(g9,g9,g19)
    c: Distance(g20) = 30
    c: Horizontal(g20)
    c: Coincident(g20,g19)
    c: Distance(g21) = 30
    c: Horizontal(g21)
    c: Coincident(g21,g7)
    c: PointOnObject(g21,g-1)
    c: Distance(g22) = 30
    c: Horizontal(g22)
    c: Coincident(g22,g8)
    c: Coincident(g23,g20)
    c: Coincident(g23,g22)
    c: Coincident(g24,g20)
    c: Coincident(g24,g21)
    c: Symmetric(g24,g24,g25)
    c: PointOnObject(g25,g10)
    c: Horizontal(g25)
    c: Coincident(g26,g25)
    c: PointOnObject(g26,g9)
    c: Horizontal(g26)
    c: Symmetric(g23,g23,g27)
    c: PointOnObject(g27,g10)
    c: Horizontal(g27)
    c: Coincident(g28,g27)
    c: PointOnObject(g28,g9)
    c: Horizontal(g28)
    c: Distance(g29) = 5
    c: Horizontal(g29)
    c: Coincident(g29,g28)
    c: Coincident(g30,g29)
    c: PointOnObject(g30,g19)
    c: Vertical(g30)
    c: Coincident(g31,g30)
    c: PointOnObject(g31,g26)
    c: Vertical(g31)
    c: Distance(g32) = 5
    c: Horizontal(g32)
    c: Coincident(g32,g25)
    c: Coincident(g33,g32)
    c: PointOnObject(g33,g19)
    c: Vertical(g33)
    c: Coincident(g34,g33)
    c: PointOnObject(g34,g28)
    c: Vertical(g34)
    c: Diameter(g35) = 3
    c: Coincident(g35,g29)
    c: Coincident(g36,g34)
    c: Equal(g35,g36)
    c: Coincident(g37,g30)
    c: Equal(g35,g37)
    c: Coincident(g38,g33)
    c: Equal(g37,g38)
    c: Coincident(g39,g31)
    c: Equal(g37,g39)
    c: Coincident(g40,g32)
    c: Equal(g39,g40)
FEATURE [PartDesign::Pad] Pad003
  Direction = (0,0,1)
  Length = 4
  Length2 = 10
  Profile = -> Sketch003
  ReferenceAxis = -> Sketch003 [N_Axis]
  Refine = true
  Suppressed = false
  Type = 0
FEATURE [PartDesign::Body] Body005  label="arm_high_002"
  AllowCompound = false
  Group = -> [Sketch003,Pad003]
  Origin = -> Origin005
  Placement = pos=(387.832,472.58,73.3) rot=(0,0,1;1.75335rad)
  Tip = -> Pad003
FEATURE [App::FeaturePython] Joint007  label="Fixed002"  # Assembly joint (typed FeaturePython)
  Activated = true
  AngleMax = 0
  AngleMin = 0
  Detach1 = false
  Detach2 = false
  Distance = 0
  Distance2 = 0
  EnableAngleMax = false
  EnableAngleMin = false
  EnableLengthMax = false
  EnableLengthMin = false
  JointType = 0 (Fixed)
  LengthMax = 0
  LengthMin = 0
  Offset2 = pos=(0,0,48) rot=(0,0,1;0rad)
  Placement2 = pos=(0,0,52) rot=(0,0,1;0rad)
  Reference1 = -> Assembly [Body004.Edge32,Body004.Edge32]
  Reference2 = -> Assembly [Body.Edge33,Body.Edge33]
FEATURE [App::FeaturePython] Joint008  label="Fixed003"  # Assembly joint (typed FeaturePython)
  Activated = true
  AngleMax = 0
  AngleMin = 0
  Detach1 = false
  Detach2 = false
  Distance = 0
  Distance2 = 0
  EnableAngleMax = false
  EnableAngleMin = false
  EnableLengthMax = false
  EnableLengthMin = false
  JointType = 0 (Fixed)
  LengthMax = 0
  LengthMin = 0
  Offset2 = pos=(0,0,40) rot=(0,0,1;0rad)
  Placement1 = pos=(5.68e-14,400.001,0) rot=(0,0,1;0rad)
  Placement2 = pos=(5.68e-14,400.001,44) rot=(0,0,1;0rad)
  Reference1 = -> Assembly [Body005.Edge17,Body005.Edge17]
  Reference2 = -> Assembly [Body001.Edge18,Body001.Edge18]
FEATURE [App::Link] Body006
  LinkPlacement = pos=(-5.52126,399.962,63.3) rot=(0,0,1;1.75335rad)
  LinkedObject = -> <external pulleys/gt2_48T_pulley_double.FCStd>#Body
  Placement = pos=(-5.52126,399.962,63.3) rot=(0,0,1;1.75335rad)
FEATURE [App::FeaturePython] Joint009  label="Revolute002"  # Assembly joint (typed FeaturePython)
  Activated = true
  AngleMax = 0
  AngleMin = 0
  Detach1 = false
  Detach2 = false
  Distance = 0
  Distance2 = 0
  EnableAngleMax = false
  EnableAngleMin = false
  EnableLengthMax = false
  EnableLengthMin = false
  JointType = 1 (Revolute)
  LengthMax = 0
  LengthMin = 0
  Placement1 = pos=(0,0,10) rot=(1,0,0;3.14159rad)
  Placement2 = pos=(5.68e-14,400.001,0) rot=(0,0,1;0rad)
  Reference1 = -> Assembly [Body006.Edge875,Body006.Edge875]
  Reference2 = -> Assembly [Body005.Edge17,Body005.Edge17]
FEATURE [App::Link] DC05_M01_DUMMY002
  LinkPlacement = pos=(0,0,106) rot=(0,1,0;3.14159rad)
  LinkedObject = -> <external srv.FCStd>#Part__Feature
  Placement = pos=(0,0,106) rot=(0,1,0;3.14159rad)
FEATURE [App::FeaturePython] Joint010  label="Fixed004"  # Assembly joint (typed FeaturePython)
  Activated = true
  AngleMax = 0
  AngleMin = 0
  Detach1 = false
  Detach2 = false
  Distance = 0
  Distance2 = 0
  EnableAngleMax = false
  EnableAngleMin = false
  EnableLengthMax = false
  EnableLengthMin = false
  JointType = 0 (Fixed)
  LengthMax = 0
  LengthMin = 0
  Offset2 = pos=(0,0,50) rot=(0,0,1;0rad)
  Placement1 = pos=(0,0,28) rot=(-0.707107,-0.707107,0;3.14159rad)
  Placement2 = pos=(0,0,78) rot=(0,0,1;1.5708rad)
  Reference1 = -> Assembly [DC05_M01_DUMMY002.Edge912,DC05_M01_DUMMY002.Edge912]
  Reference2 = -> Assembly [DC05_M01_DUMMY.Edge915,DC05_M01_DUMMY.Edge915]
FEATURE [App::Link] DC05_M01_DUMMY003
  LinkPlacement = pos=(-0.487674,37.9968,98.05) rot=(0.999976,0.006902,0;3.14159rad)
  LinkedObject = -> <external srv.FCStd>#Part__Feature
  Placement = pos=(-0.487674,37.9968,98.05) rot=(0.999976,0.006902,0;3.14159rad)
FEATURE [App::FeaturePython] Joint011  label="Fixed005"  # Assembly joint (typed FeaturePython)
  Activated = true
  AngleMax = 0
  AngleMin = 0
  Detach1 = false
  Detach2 = false
  Distance = 0
  Distance2 = 0
  EnableAngleMax = false
  EnableAngleMin = false
  EnableLengthMax = false
  EnableLengthMin = false
  JointType = 0 (Fixed)
  LengthMax = 0
  LengthMin = 0
  Offset2 = pos=(0,0,-33) rot=(0,0,1;0rad)
  Placement1 = pos=(0,0,28) rot=(0,0,1;1.5708rad)
  Placement2 = pos=(0,0,61) rot=(-0.707107,-0.707107,0;3.14159rad)
  Reference1 = -> Assembly [DC05_M01_DUMMY003.Edge915,DC05_M01_DUMMY003.Edge915]
  Reference2 = -> Assembly [DC05_M01_DUMMY001.Edge912,DC05_M01_DUMMY001.Edge912]
FEATURE [App::Link] Body007
  LinkPlacement = pos=(-0.487674,37.9968,68.55) rot=(0.71197,-0.70221,0;3.14159rad)
  LinkedObject = -> <external pulleys/gt2_24T_pulley_open.FCStd>#Body
  Placement = pos=(-0.487674,37.9968,68.55) rot=(0.71197,-0.70221,0;3.14159rad)
FEATURE [App::FeaturePython] Joint012  label="Revolute003"  # Assembly joint (typed FeaturePython)
  Activated = true
  AngleMax = 0
  AngleMin = 0
  Detach1 = false
  Detach2 = false
  Distance = 0
  Distance2 = 0
  EnableAngleMax = false
  EnableAngleMin = false
  EnableLengthMax = false
  EnableLengthMin = false
  JointType = 1 (Revolute)
  LengthMax = 0
  LengthMin = 0
  Placement1 = pos=(0,0,-6) rot=(-1,0,0;3.14159rad)
  Placement2 = pos=(0,0,23.5) rot=(0,0,1;1.5708rad)
  Reference1 = -> Assembly [Body007.Edge529,Body007.Edge529]
  Reference2 = -> Assembly [DC05_M01_DUMMY003.Edge889,DC05_M01_DUMMY003.Edge889]
FEATURE [App::Link] Body008  label="Body001"
  LinkPlacement = pos=(-0.487674,37.9968,38.55) rot=(0,0,-1;1.55699rad)
  LinkedObject = -> <external pulleys/gt2_24T_pulley_open.FCStd>#Body001
  Placement = pos=(-0.487674,37.9968,38.55) rot=(0,0,-1;1.55699rad)
FEATURE [App::FeaturePython] Joint013  label="Fixed006"  # Assembly joint (typed FeaturePython)
  Activated = true
  AngleMax = 0
  AngleMin = 0
  Detach1 = false
  Detach2 = false
  Distance = 0
  Distance2 = 0
  EnableAngleMax = false
  EnableAngleMin = false
  EnableLengthMax = false
  EnableLengthMin = false
  JointType = 0 (Fixed)
  LengthMax = 0
  LengthMin = 0
  Placement1 = pos=(0,0,8) rot=(0,0,1;0rad)
  Placement2 = pos=(0,0,8) rot=(1,0,0;3.14159rad)
  Reference1 = -> Assembly [Body008.Edge8,Body008.Edge8]
  Reference2 = -> Assembly [Body002.Edge520,Body002.Edge520]
FEATURE [App::Link] Body009
  LinkPlacement = pos=(-0.487674,37.9968,68.55) rot=(0.71197,-0.70221,0;3.14159rad)
  LinkedObject = -> <external pulleys/gt2_24T_pulley_open.FCStd>#Body001
  Placement = pos=(-0.487674,37.9968,68.55) rot=(0.71197,-0.70221,0;3.14159rad)
FEATURE [App::FeaturePython] Joint014  label="Fixed007"  # Assembly joint (typed FeaturePython)
  Activated = true
  AngleMax = 0
  AngleMin = 0
  Detach1 = false
  Detach2 = false
  Distance = 0
  Distance2 = 0
  EnableAngleMax = false
  EnableAngleMin = false
  EnableLengthMax = false
  EnableLengthMin = false
  JointType = 0 (Fixed)
  LengthMax = 0
  LengthMin = 0
  Placement1 = pos=(0,0,8) rot=(0,0,1;0rad)
  Placement2 = pos=(0,0,8) rot=(1,0,0;3.14159rad)
  Reference1 = -> Assembly [Body009.Edge8,Body009.Edge8]
  Reference2 = -> Assembly [Body007.Edge520,Body007.Edge520]
FEATURE [Assembly::JointGroup] Joints
  Group = -> [GroundedJoint,Joint,Joint001,Joint002,Joint003,Joint004,Joint005,Joint006,Joint007,Joint008,Joint009,Joint010,Joint011,Joint012,Joint013,Joint014]
FEATURE [Assembly::AssemblyObject] Assembly
  Group = -> [Joints,Body,Body004,Body001,Body005,DC05_M01_DUMMY,GroundedJoint,Joint,Joint001,DC05_M01_DUMMY001,Joint002,Joint003,Joint004,Body002,Joint005,Body003,Joint006,Joint007,Joint008,Body006,Joint009,DC05_M01_DUMMY002,Joint010,DC05_M01_DUMMY003,Joint011,Body007,Joint012,Body008,Joint013,Body009,Joint014]
  Origin = -> Origin003
  Type = Assembly

RESOLVED EXTERNAL PARTS (link-assembly join: the EXTERNAL_REF files above that resolve inside this repo's crawl, each included once):
---- part pulleys/gt2_24T_pulley_open.FCStd = doc fcstd_ee15d791d3af ----
FCSTD DOCUMENT  (FreeCAD 1.0R39109 (Git))
Label: gt2_24T_pulley_open
License: All rights reserved
LicenseURL: https://en.wikipedia.org/wiki/All_rights_reserved
objects: Sketcher::SketchObject×8, PartDesign::Chamfer×7, PartDesign::Pad×4, PartDesign::Pocket×4, PartDesign::Body×2, Part::FeaturePython×1, PartDesign::FeatureBase×1, PartDesign::ShapeBinder×1, App::Part×1
note: 67 computed .brp shape members not serialized (recipe doc carries the construction recipe); baked Part::Feature solids carry a one-line shape summary decoded from their .brp

FEATURE [Part::FeaturePython] TimingGear  # WARN: FeaturePython — macro-defined, semantics opaque (R4)
  AttacherType = Attacher::AttachEngine3D
  h = 0.75
  height = 8
  num_teeth = 24
  offset = 0.4
  pitch = 2
  r0 = 0.555
  r1 = 1
  rs = 0.15
  type = 0
  u = 0.254
  version = 1.3.0
FEATURE [PartDesign::FeatureBase] BaseFeature
  BaseFeature = -> TimingGear
  Suppressed = false
FEATURE [Sketcher::SketchObject] Sketch
  ArcFitTolerance = 1e-06
  AttachmentSupport = -> [BaseFeature]
  FullyConstrained = true
  MakeInternals = false
  MapMode = 5
  Placement = pos=(0,0,0) rot=(1,0,0;3.14159rad)
  sketch-geometry (1):
    g0: Circle CenterX=0 CenterY=0 CenterZ=0 NormalX=0 NormalY=0 NormalZ=1 AngleXU=0 Radius=9
  constraints (2):
    c: Diameter(g0) = 18
    c: Coincident(g0,g-1)
FEATURE [PartDesign::Pad] Pad
  BaseFeature = -> BaseFeature
  Direction = (0,0,-1)
  Length = 2
  Length2 = 10
  Profile = -> Sketch
  ReferenceAxis = -> Sketch [N_Axis]
  Refine = true
  Suppressed = false
  Type = 0
FEATURE [Sketcher::SketchObject] Sketch001
  ArcFitTolerance = 1e-06
  AttachmentSupport = -> [Pad]
  FullyConstrained = true
  MakeInternals = false
  MapMode = 5
  Placement = pos=(0,0,-2) rot=(1,0,0;3.14159rad)
  sketch-geometry (1):
    g0: Circle CenterX=0 CenterY=0 CenterZ=0 NormalX=0 NormalY=0 NormalZ=1 AngleXU=0 Radius=14
  constraints (2):
    c: Diameter(g0) = 28
    c: Coincident(g0,g-1)
FEATURE [PartDesign::Pad] Pad001
  BaseFeature = -> Pad
  Direction = (0,0,-1)
  Length = 3
  Length2 = 10
  Profile = -> Sketch001
  ReferenceAxis = -> Sketch001 [N_Axis]
  Refine = true
  Suppressed = false
  Type = 0
FEATURE [Sketcher::SketchObject] Sketch002
  ArcFitTolerance = 1e-06
  AttachmentSupport = -> [Pad001]
  FullyConstrained = false
  MakeInternals = false
  MapMode = 5
  Placement = pos=(0,0,-5) rot=(1,0,0;3.14159rad)
  sketch-geometry (7):
    g0: Circle [constr] CenterX=0 CenterY=5.078e-13 CenterZ=0 NormalX=0 NormalY=0 NormalZ=1 AngleXU=0 Radius=11
    g1: LineSegment [constr] StartX=0 StartY=5.078e-13 StartZ=0 EndX=0 EndY=11 EndZ=0
    g2: Circle CenterX=0 CenterY=11 CenterZ=0 NormalX=0 NormalY=0 NormalZ=1 AngleXU=0 Radius=5.092e-13
    g3: Circle CenterX=0 CenterY=11 CenterZ=0 NormalX=0 NormalY=0 NormalZ=1 AngleXU=0 Radius=1.25
    g4: Circle CenterX=-11 CenterY=0 CenterZ=0 NormalX=0 NormalY=0 NormalZ=1 AngleXU=0 Radius=1.25
    g5: Circle CenterX=0 CenterY=-11 CenterZ=0 NormalX=0 NormalY=0 NormalZ=1 AngleXU=0 Radius=1.25
    g6: Circle CenterX=11 CenterY=0 CenterZ=0 NormalX=0 NormalY=0 NormalZ=1 AngleXU=0 Radius=1.25
  constraints (12):
    c: Diameter(g0) = 22
    c: Coincident(g0,g-1)
    c: Coincident(g1,g0)
    c: PointOnObject(g1,g0)
    c: Vertical(g1)
    c: Coincident(g2,g1)
    c: Tangent(g2,g0)
    c: Coincident(g3,g1)
    c: Diameter(g3) = 2.5
    c: Diameter(g4) = 2.5
    c: Diameter(g5) = 2.5
    c: Diameter(g6) = 2.5
FEATURE [PartDesign::Pocket] Pocket
  BaseFeature = -> Pad001
  Direction = (0,0,1)
  Length = 19
  Length2 = 5
  Profile = -> Sketch002
  ReferenceAxis = -> Sketch002 [N_Axis]
  Refine = true
  Suppressed = false
  Type = 0
FEATURE [Sketcher::SketchObject] Sketch003
  ArcFitTolerance = 1e-06
  AttachmentSupport = -> [Pocket]
  FullyConstrained = true
  MakeInternals = false
  MapMode = 5
  Placement = pos=(0,0,-5) rot=(1,0,0;3.14159rad)
  sketch-geometry (1):
    g0: Circle CenterX=0 CenterY=0 CenterZ=0 NormalX=0 NormalY=0 NormalZ=1 AngleXU=0 Radius=6
  constraints (2):
    c: Coincident(g0,g-1)
    c: Diameter(g0) = 12
FEATURE [PartDesign::Pocket] Pocket001
  BaseFeature = -> Pocket
  Direction = (0,0,1)
  Length = 5
  Length2 = 5
  Profile = -> Sketch003
  ReferenceAxis = -> Sketch003 [N_Axis]
  Refine = true
  Suppressed = false
  Type = 0
FEATURE [Sketcher::SketchObject] Sketch004
  ArcFitTolerance = 1e-06
  AttachmentSupport = -> [Pocket001]
  FullyConstrained = true
  MakeInternals = false
  MapMode = 5
  Placement = pos=(0,0,-9e-16) rot=(1,0,0;3.14159rad)
  sketch-geometry (1):
    g0: Circle CenterX=0 CenterY=0 CenterZ=0 NormalX=0 NormalY=0 NormalZ=1 AngleXU=0 Radius=1.75
  constraints (2):
    c: Coincident(g0,g-1)
    c: Diameter(g0) = 3.5
FEATURE [PartDesign::Pocket] Pocket002
  BaseFeature = -> Pocket001
  Direction = (0,0,1)
  Length = 20
  Length2 = 5
  Profile = -> Sketch004
  ReferenceAxis = -> Sketch004 [N_Axis]
  Refine = true
  Suppressed = false
  Type = 0
FEATURE [PartDesign::Chamfer] Chamfer
  Angle = 45
  Base = -> Pocket002 [Edge437]
  BaseFeature = -> Pocket002
  ChamferType = 0
  FlipDirection = false
  Refine = true
  Size = 4.2
  Size2 = 1
  SupportTransform = false
  Suppressed = false
  UseAllEdges = false
FEATURE [PartDesign::Chamfer] Chamfer001
  Angle = 45
  Base = -> Chamfer [Edge441]
  BaseFeature = -> Chamfer
  ChamferType = 0
  FlipDirection = false
  Refine = true
  Size = 0.5
  Size2 = 1
  SupportTransform = false
  Suppressed = false
  UseAllEdges = false
FEATURE [PartDesign::Chamfer] Chamfer002
  Angle = 45
  Base = -> Chamfer001 [Edge439,Edge447]
  BaseFeature = -> Chamfer001
  ChamferType = 0
  FlipDirection = false
  Refine = true
  Size = 0.5
  Size2 = 1
  SupportTransform = false
  Suppressed = false
  UseAllEdges = false
FEATURE [PartDesign::Chamfer] Chamfer003
  Angle = 45
  Base = -> Chamfer002 [Edge22,Edge15,Edge17,Edge15,Edge9,Edge11]
  BaseFeature = -> Chamfer002
  ChamferType = 0
  FlipDirection = false
  Refine = true
  Size = 0.5
  Size2 = 1
  SupportTransform = false
  Suppressed = false
  UseAllEdges = false
FEATURE [PartDesign::Chamfer] Chamfer004
  Angle = 45
  Base = -> Chamfer003 [Edge473]
  BaseFeature = -> Chamfer003
  ChamferType = 0
  FlipDirection = false
  Refine = true
  Size = 0.5
  Size2 = 1
  SupportTransform = false
  Suppressed = false
  UseAllEdges = false
FEATURE [PartDesign::ShapeBinder] CopyChamfer004
  TraceSupport = false
FEATURE [Sketcher::SketchObject] Sketch005
  ArcFitTolerance = 1e-06
  AttachmentSupport = -> [CopyChamfer004]
  FullyConstrained = true
  MakeInternals = false
  MapMode = 5
  Placement = pos=(0,0,8) rot=(0,0,1;0rad)
  sketch-geometry (1):
    g0: Circle CenterX=0 CenterY=0 CenterZ=0 NormalX=0 NormalY=0 NormalZ=1 AngleXU=0 Radius=11
  constraints (2):
    c: Diameter(g0) = 22
    c: Coincident(g0,g-1)
FEATURE [PartDesign::Pad] Pad002
  Direction = (0,0,1)
  Length = 2
  Length2 = 10
  Profile = -> Sketch005
  ReferenceAxis = -> Sketch005 [N_Axis]
  Refine = true
  Suppressed = false
  Type = 0
FEATURE [Sketcher::SketchObject] Sketch006
  ArcFitTolerance = 1e-06
  AttachmentSupport = -> [Pad002]
  FullyConstrained = true
  MakeInternals = false
  MapMode = 5
  Placement = pos=(0,0,10) rot=(0,0,1;0rad)
  sketch-geometry (1):
    g0: Circle CenterX=0 CenterY=0 CenterZ=0 NormalX=0 NormalY=0 NormalZ=1 AngleXU=0 Radius=1.5
  constraints (2):
    c: Diameter(g0) = 3
    c: Coincident(g0,g-1)
FEATURE [PartDesign::Pocket] Pocket003
  BaseFeature = -> Pad002
  Direction = (0,0,-1)
  Length = 15
  Length2 = 5
  Profile = -> Sketch006
  ReferenceAxis = -> Sketch006 [N_Axis]
  Refine = true
  Suppressed = false
  Type = 0
FEATURE [PartDesign::Chamfer] Chamfer005
  Angle = 45
  Base = -> Pocket003 [Edge2,Edge3,Edge5,Edge4]
  BaseFeature = -> Pocket003
  ChamferType = 0
  FlipDirection = false
  Refine = true
  Size = 0.5
  Size2 = 1
  SupportTransform = false
  Suppressed = false
  UseAllEdges = false
FEATURE [PartDesign::Body] Body001
  AllowCompound = false
  Group = -> [CopyChamfer004,Sketch005,Pad002,Sketch006,Pocket003,Chamfer005]
  Origin = -> Origin001
  Tip = -> Chamfer005
FEATURE [Sketcher::SketchObject] Sketch007
  ArcFitTolerance = 1e-06
  AttachmentSupport = -> [Chamfer004]
  ExternalGeometry = -> [Chamfer004]
  FullyConstrained = true
  MakeInternals = false
  MapMode = 5
  Placement = pos=(0,0,-2) rot=(0,0,1;0rad)
  sketch-geometry (25):
    g0: Circle [constr] CenterX=0 CenterY=0 CenterZ=0 NormalX=0 NormalY=0 NormalZ=1 AngleXU=0 Radius=9
    g1: LineSegment [constr] StartX=0 StartY=0 StartZ=0 EndX=7.79423 EndY=-4.5 EndZ=0
    g2: LineSegment [constr] StartX=0 StartY=0 StartZ=0 EndX=4.5 EndY=-7.79423 EndZ=0
    g3: LineSegment StartX=7.79423 StartY=-4.5 StartZ=0 EndX=11.6913 EndY=-6.75 EndZ=0
    g4: LineSegment StartX=4.5 StartY=-7.79423 StartZ=0 EndX=6.75 EndY=-11.6913 EndZ=0
    g5: LineSegment [constr] StartX=0 StartY=0 StartZ=0 EndX=7.79423 EndY=4.5 EndZ=0
    g6: LineSegment [constr] StartX=0 StartY=0 StartZ=0 EndX=4.5 EndY=7.79423 EndZ=0
    g7: LineSegment [constr] StartX=0 StartY=0 StartZ=0 EndX=-4.5 EndY=7.79423 EndZ=0
    g8: LineSegment [constr] StartX=0 StartY=0 StartZ=0 EndX=-7.79423 EndY=4.5 EndZ=0
    g9: LineSegment [constr] StartX=0 StartY=0 StartZ=0 EndX=-7.79423 EndY=-4.5 EndZ=0
    g10: LineSegment [constr] StartX=0 StartY=0 StartZ=0 EndX=-4.5 EndY=-7.79423 EndZ=0
    g11: LineSegment StartX=7.79423 StartY=4.5 StartZ=0 EndX=11.6913 EndY=6.75 EndZ=0
    g12: LineSegment StartX=4.5 StartY=7.79423 StartZ=0 EndX=6.75 EndY=11.6913 EndZ=0
    g13: LineSegment StartX=-4.5 StartY=7.79423 StartZ=0 EndX=-6.75 EndY=11.6913 EndZ=0
    g14: LineSegment StartX=-7.79423 StartY=4.5 StartZ=0 EndX=-11.6913 EndY=6.75 EndZ=0
    g15: LineSegment StartX=-7.79423 StartY=-4.5 StartZ=0 EndX=-11.6913 EndY=-6.75 EndZ=0
    g16: LineSegment StartX=-4.5 StartY=-7.79423 StartZ=0 EndX=-6.75 EndY=-11.6913 EndZ=0
    g17: ArcOfCircle CenterX=0 CenterY=0 CenterZ=0 NormalX=0 NormalY=0 NormalZ=1 AngleXU=0 Radius=9 StartAngle=0.523599 EndAngle=1.0472
    g18: ArcOfCircle CenterX=0 CenterY=0 CenterZ=0 NormalX=0 NormalY=0 NormalZ=1 AngleXU=0 Radius=9 StartAngle=2.0944 EndAngle=2.61799
    g19: ArcOfCircle CenterX=0 CenterY=0 CenterZ=0 NormalX=0 NormalY=0 NormalZ=1 AngleXU=0 Radius=9 StartAngle=3.66519 EndAngle=4.18879
    g20: ArcOfCircle CenterX=0 CenterY=0 CenterZ=0 NormalX=0 NormalY=0 NormalZ=1 AngleXU=0 Radius=9 StartAngle=5.23599 EndAngle=5.75959
    g21: ArcOfCircle CenterX=0 CenterY=0 CenterZ=0 NormalX=0 NormalY=0 NormalZ=1 AngleXU=0 Radius=13.5 StartAngle=0.523599 EndAngle=1.0472
    g22: ArcOfCircle CenterX=0 CenterY=0 CenterZ=0 NormalX=0 NormalY=0 NormalZ=1 AngleXU=0 Radius=13.5 StartAngle=2.0944 EndAngle=2.61799
    g23: ArcOfCircle CenterX=0 CenterY=0 CenterZ=0 NormalX=0 NormalY=0 NormalZ=1 AngleXU=0 Radius=13.5 StartAngle=3.66519 EndAngle=4.18879
    g24: ArcOfCircle CenterX=0 CenterY=0 CenterZ=0 NormalX=0 NormalY=0 NormalZ=1 AngleXU=0 Radius=13.5 StartAngle=5.23599 EndAngle=5.75959
  constraints (80):
    c: Coincident(g0,g-1)
    c: Diameter(g0) = 18
    c: Coincident(g1,g0)
    c: PointOnObject(g1,g0)
    c: Angle(g1,g-1) = 0.523599
    c: Coincident(g2,g0)
    c: PointOnObject(g2,g0)
    c: Angle(g2,g1) = 0.523599
    c: Coincident(g3,g1)
    c: PointOnObject(g3,g-4)
    c: Parallel(g1,g3)
    c: Coincident(g4,g2)
    c: PointOnObject(g4,g-4)
    c: Parallel(g2,g4)
    c: Coincident(g5,g0)
    c: PointOnObject(g5,g0)
    c: Coincident(g6,g0)
    c: PointOnObject(g6,g0)
    c: Coincident(g7,g0)
    c: PointOnObject(g7,g0)
    c: Coincident(g8,g0)
    c: PointOnObject(g8,g0)
    c: Coincident(g9,g0)
    c: PointOnObject(g9,g0)
    c: Coincident(g10,g0)
    c: PointOnObject(g10,g0)
    c: Angle(g-1,g5) = 0.523599
    c: Angle(g5,g6) = 0.523599
    c: Angle(g6,g7) = 1.0472
    c: Angle(g7,g8) = 0.523599
    c: Angle(g8,g9) = 1.0472
    c: Angle(g9,g10) = 0.523599
    c: Coincident(g11,g5)
    c: PointOnObject(g11,g-4)
    c: Coincident(g12,g6)
    c: PointOnObject(g12,g-4)
    c: Coincident(g13,g7)
    c: PointOnObject(g13,g-4)
    c: Coincident(g14,g8)
    c: PointOnObject(g14,g-4)
    c: Coincident(g15,g9)
    c: PointOnObject(g15,g-4)
    c: Coincident(g16,g10)
    c: PointOnObject(g16,g-4)
    c: Parallel(g5,g11)
    c: Parallel(g6,g12)
    c: Parallel(g7,g13)
    c: Parallel(g8,g14)
    c: Parallel(g9,g15)
    c: Parallel(g10,g16)
    c: Coincident(g17,g0)
    c: Coincident(g20,g1)
    c: PointOnObject(g17,g5)
    c: Equal(g17,g18)
    c: PointOnObject(g17,g6)
    c: PointOnObject(g18,g7)
    c: Coincident(g17,g18)
    c: Equal(g18,g19)
    c: PointOnObject(g18,g8)
    c: PointOnObject(g19,g9)
    c: Coincident(g18,g19)
    c: Equal(g19,g20)
    c: PointOnObject(g19,g10)
    c: PointOnObject(g20,g2)
    c: Coincident(g19,g20)
    c: Coincident(g21,g0)
    c: Coincident(g21,g11)
    c: PointOnObject(g24,g3)
    c: Equal(g21,g22)
    c: PointOnObject(g21,g12)
    c: PointOnObject(g22,g13)
    c: Coincident(g21,g22)
    c: Equal(g22,g23)
    c: PointOnObject(g22,g14)
    c: PointOnObject(g23,g15)
    c: Coincident(g22,g23)
    c: Equal(g23,g24)
    c: PointOnObject(g23,g16)
    c: PointOnObject(g24,g4)
    c: Coincident(g23,g24)
FEATURE [PartDesign::Pad] Pad003
  BaseFeature = -> Chamfer004
  Direction = (0,0,1)
  Length = 1.5
  Length2 = 10
  Profile = -> Sketch007
  ReferenceAxis = -> Sketch007 [N_Axis]
  Refine = true
  Suppressed = false
  Type = 0
FEATURE [PartDesign::Chamfer] Chamfer006
  Angle = 45
  Base = -> Pad003 [Edge453,Edge471,Edge465,Edge459]
  BaseFeature = -> Pad003
  ChamferType = 1
  FlipDirection = false
  Refine = true
  Size = 4.4
  Size2 = 1.4
  SupportTransform = false
  Suppressed = false
  UseAllEdges = false
FEATURE [PartDesign::Body] Body
  AllowCompound = false
  BaseFeature = -> TimingGear
  Group = -> [BaseFeature,Sketch,Pad,Sketch001,Pad001,Sketch002,Pocket,Sketch003,Pocket001,Sketch004,Pocket002,Chamfer,Chamfer001,Chamfer002,Chamfer003,Chamfer004,Sketch007,Pad003,Chamfer006]
  Origin = -> Origin
  Tip = -> Chamfer006
FEATURE [App::Part] Part
  Group = -> [TimingGear,Body,Body001]
  Origin = -> Origin002
---- part pulleys/gt2_48T_pulley.FCStd = doc fcstd_034fdf5fdbef ----
FCSTD DOCUMENT  (FreeCAD 1.0R39109 (Git))
Label: gt2_48T_pulley
License: All rights reserved
LicenseURL: https://en.wikipedia.org/wiki/All_rights_reserved
objects: Sketcher::SketchObject×6, PartDesign::Chamfer×5, PartDesign::Pocket×4, PartDesign::Pad×2, Part::FeaturePython×1, PartDesign::FeatureBase×1, PartDesign::Body×1
note: 49 computed .brp shape members not serialized (recipe doc carries the construction recipe); baked Part::Feature solids carry a one-line shape summary decoded from their .brp

FEATURE [Part::FeaturePython] TimingGear  # WARN: FeaturePython — macro-defined, semantics opaque (R4)
  AttacherType = Attacher::AttachEngine3D
  h = 0.75
  height = 8
  num_teeth = 48
  offset = 0.4
  pitch = 2
  r0 = 0.555
  r1 = 1
  rs = 0.15
  type = 0
  u = 0.254
  version = 1.3.0
FEATURE [PartDesign::FeatureBase] BaseFeature
  BaseFeature = -> TimingGear
  Suppressed = false
FEATURE [Sketcher::SketchObject] Sketch
  ArcFitTolerance = 1e-06
  AttachmentSupport = -> [BaseFeature]
  FullyConstrained = true
  MakeInternals = false
  MapMode = 5
  Placement = pos=(0,0,0) rot=(1,0,0;3.14159rad)
  sketch-geometry (1):
    g0: Circle CenterX=0 CenterY=0 CenterZ=0 NormalX=0 NormalY=0 NormalZ=1 AngleXU=0 Radius=19
  constraints (2):
    c: Diameter(g0) = 38
    c: Coincident(g0,g-1)
FEATURE [PartDesign::Pad] Pad
  BaseFeature = -> BaseFeature
  Direction = (0,0,-1)
  Length = 2
  Length2 = 10
  Profile = -> Sketch
  ReferenceAxis = -> Sketch [N_Axis]
  Refine = true
  Suppressed = false
  Type = 0
FEATURE [Sketcher::SketchObject] Sketch001
  ArcFitTolerance = 1e-06
  AttachmentSupport = -> [Pad]
  FullyConstrained = false
  MakeInternals = false
  MapMode = 5
  Placement = pos=(0,0,-2) rot=(1,0,0;3.14159rad)
  sketch-geometry (6):
    g0: Circle [constr] CenterX=0 CenterY=0 CenterZ=0 NormalX=0 NormalY=0 NormalZ=1 AngleXU=0 Radius=11
    g1: LineSegment [constr] StartX=0 StartY=0 StartZ=0 EndX=0 EndY=11 EndZ=0
    g2: Circle CenterX=0 CenterY=11 CenterZ=0 NormalX=0 NormalY=0 NormalZ=1 AngleXU=0 Radius=1.5
    g3: Circle CenterX=-11 CenterY=0 CenterZ=0 NormalX=0 NormalY=0 NormalZ=1 AngleXU=0 Radius=1.5
    g4: Circle CenterX=0 CenterY=-11 CenterZ=0 NormalX=0 NormalY=0 NormalZ=1 AngleXU=0 Radius=1.5
    g5: Circle CenterX=11 CenterY=0 CenterZ=0 NormalX=0 NormalY=0 NormalZ=1 AngleXU=0 Radius=1.5
  constraints (10):
    c: Diameter(g0) = 22
    c: Coincident(g0,g-1)
    c: Coincident(g1,g0)
    c: PointOnObject(g1,g0)
    c: Vertical(g1)
    c: Coincident(g2,g1)
    c: Diameter(g2) = 3
    c: Equal(g5,g2)
    c: Equal(g4,g5)
    c: Equal(g3,g4)
FEATURE [Sketcher::SketchObject] Sketch002
  ArcFitTolerance = 1e-06
  AttachmentSupport = -> [Pad]
  ExternalGeometry = -> [Pad]
  FullyConstrained = true
  MakeInternals = false
  MapMode = 5
  Placement = pos=(0,0,8) rot=(0,0,1;0rad)
  sketch-geometry (1):
    g0: Circle CenterX=0 CenterY=0 CenterZ=0 NormalX=0 NormalY=0 NormalZ=1 AngleXU=0 Radius=19
  constraints (2):
    c: Coincident(g0,g-1)
    c: Diameter(g0) = 38
FEATURE [PartDesign::Pad] Pad001
  BaseFeature = -> Pad
  Direction = (0,0,1)
  Length = 2
  Length2 = 10
  Profile = -> Sketch002
  ReferenceAxis = -> Sketch002 [N_Axis]
  Refine = true
  Suppressed = false
  Type = 0
FEATURE [PartDesign::Pocket] Pocket
  BaseFeature = -> Pad001
  Direction = (0,0,1)
  Length = 29
  Length2 = 5
  Profile = -> Sketch001
  ReferenceAxis = -> Sketch001 [N_Axis]
  Refine = true
  Suppressed = false
  Type = 0
FEATURE [Sketcher::SketchObject] Sketch003
  ArcFitTolerance = 1e-06
  AttachmentSupport = -> [Pocket]
  FullyConstrained = true
  MakeInternals = false
  MapMode = 5
  Placement = pos=(0,0,-2) rot=(1,0,0;3.14159rad)
  sketch-geometry (1):
    g0: Circle CenterX=0 CenterY=0 CenterZ=0 NormalX=0 NormalY=0 NormalZ=1 AngleXU=0 Radius=3
  constraints (2):
    c: Diameter(g0) = 6
    c: Coincident(g0,g-1)
FEATURE [PartDesign::Pocket] Pocket001
  BaseFeature = -> Pocket
  Direction = (0,0,1)
  Length = 17
  Length2 = 5
  Profile = -> Sketch003
  ReferenceAxis = -> Sketch003 [N_Axis]
  Refine = true
  Suppressed = false
  Type = 0
FEATURE [PartDesign::Chamfer] Chamfer
  Angle = 45
  Base = -> Pocket001 [Edge11,Edge297,Edge870,Edge586,Edge871,Edge874,Edge875,Edge872]
  BaseFeature = -> Pocket001
  ChamferType = 0
  FlipDirection = false
  Refine = true
  Size = 0.5
  Size2 = 1
  SupportTransform = false
  Suppressed = false
  UseAllEdges = false
FEATURE [Sketcher::SketchObject] Sketch004
  ArcFitTolerance = 1e-06
  AttachmentSupport = -> [Chamfer]
  ExternalGeometry = -> [Chamfer]
  FullyConstrained = false
  MakeInternals = false
  MapMode = 5
  Placement = pos=(0,0,10) rot=(0,0,1;0rad)
  sketch-geometry (28):
    g0: LineSegment StartX=0 StartY=14 StartZ=0 EndX=-2.59808 EndY=12.5 EndZ=0
    g1: LineSegment StartX=-2.59808 StartY=12.5 StartZ=0 EndX=-2.59808 EndY=9.5 EndZ=0
    g2: LineSegment StartX=-2.59808 StartY=9.5 StartZ=0 EndX=-4e-16 EndY=8 EndZ=0
    g3: LineSegment StartX=-4e-16 StartY=8 StartZ=0 EndX=2.59808 EndY=9.5 EndZ=0
    g4: LineSegment StartX=2.59808 StartY=9.5 StartZ=0 EndX=2.59808 EndY=12.5 EndZ=0
    g5: LineSegment StartX=2.59808 StartY=12.5 StartZ=0 EndX=0 EndY=14 EndZ=0
    g6: Circle [constr] CenterX=0 CenterY=11 CenterZ=0 NormalX=0 NormalY=0 NormalZ=1 AngleXU=0 Radius=3
    g7: LineSegment StartX=11 StartY=3 StartZ=0 EndX=8.40192 EndY=1.5 EndZ=0
    g8: LineSegment StartX=8.40192 StartY=1.5 StartZ=0 EndX=8.40192 EndY=-1.5 EndZ=0
    g9: LineSegment StartX=8.40192 StartY=-1.5 StartZ=0 EndX=11 EndY=-3 EndZ=0
    g10: LineSegment StartX=11 StartY=-3 StartZ=0 EndX=13.5981 EndY=-1.5 EndZ=0
    g11: LineSegment StartX=13.5981 StartY=-1.5 StartZ=0 EndX=13.5981 EndY=1.5 EndZ=0
    g12: LineSegment StartX=13.5981 StartY=1.5 StartZ=0 EndX=11 EndY=3 EndZ=0
    g13: Circle [constr] CenterX=11 CenterY=0 CenterZ=0 NormalX=0 NormalY=0 NormalZ=1 AngleXU=0 Radius=3
    g14: LineSegment StartX=0 StartY=-8 StartZ=0 EndX=-2.59808 EndY=-9.5 EndZ=0
    g15: LineSegment StartX=-2.59808 StartY=-9.5 StartZ=0 EndX=-2.59808 EndY=-12.5 EndZ=0
    g16: LineSegment StartX=-2.59808 StartY=-12.5 StartZ=0 EndX=-4e-16 EndY=-14 EndZ=0
    g17: LineSegment StartX=-4e-16 StartY=-14 StartZ=0 EndX=2.59808 EndY=-12.5 EndZ=0
    g18: LineSegment StartX=2.59808 StartY=-12.5 StartZ=0 EndX=2.59808 EndY=-9.5 EndZ=0
    g19: LineSegment StartX=2.59808 StartY=-9.5 StartZ=0 EndX=0 EndY=-8 EndZ=0
    g20: Circle [constr] CenterX=0 CenterY=-11 CenterZ=0 NormalX=0 NormalY=0 NormalZ=1 AngleXU=0 Radius=3
    g21: LineSegment StartX=-11 StartY=3 StartZ=0 EndX=-13.5981 EndY=1.5 EndZ=0
    g22: LineSegment StartX=-13.5981 StartY=1.5 StartZ=0 EndX=-13.5981 EndY=-1.5 EndZ=0
    g23: LineSegment StartX=-13.5981 StartY=-1.5 StartZ=0 EndX=-11 EndY=-3 EndZ=0
    g24: LineSegment StartX=-11 StartY=-3 StartZ=0 EndX=-8.40192 EndY=-1.5 EndZ=0
    g25: LineSegment StartX=-8.40192 StartY=-1.5 StartZ=0 EndX=-8.40192 EndY=1.5 EndZ=0
    g26: LineSegment StartX=-8.40192 StartY=1.5 StartZ=0 EndX=-11 EndY=3 EndZ=0
    g27: Circle [constr] CenterX=-11 CenterY=0 CenterZ=0 NormalX=0 NormalY=0 NormalZ=1 AngleXU=0 Radius=3
  constraints (62):
    c: Coincident(g0,g1)
    c: Coincident(g1,g2)
    c: Coincident(g2,g3)
    c: Coincident(g3,g4)
    c: Coincident(g4,g5)
    c: Coincident(g5,g0)
    c: Equal(g0, g1-g5) x5
    c: PointOnObject(g0,g6)
    c: PointOnObject(g1,g6)
    c: PointOnObject(g2,g6)
    c: PointOnObject(g3,g6)
    c: PointOnObject(g4,g6)
    c: PointOnObject(g5,g6)
    c: Radius(g6) = 3
    c: Coincident(g6,g-3)
    c: PointOnObject(g5,g-2)
    c: Coincident(g7,g8)
    c: Coincident(g8,g9)
    c: Coincident(g9,g10)
    c: Coincident(g10,g11)
    c: Coincident(g11,g12)
    c: Coincident(g12,g7)
    c: Equal(g7, g8-g12) x5
    c: PointOnObject(g7,g13)
    c: PointOnObject(g8,g13)
    c: PointOnObject(g9,g13)
    c: PointOnObject(g10,g13)
    c: PointOnObject(g11,g13)
    c: PointOnObject(g12,g13)
    c: Radius(g13) = 3
    c: Coincident(g13,g-5)
    c: Coincident(g14,g15)
    c: Coincident(g15,g16)
    c: Coincident(g16,g17)
    c: Coincident(g17,g18)
    c: Coincident(g18,g19)
    c: Coincident(g19,g14)
    c: Equal(g14, g15-g19) x5
    c: PointOnObject(g14,g20)
    c: PointOnObject(g15,g20)
    c: PointOnObject(g16,g20)
    c: PointOnObject(g17,g20)
    c: PointOnObject(g18,g20)
    c: PointOnObject(g19,g20)
    c: Radius(g20) = 3
    c: Coincident(g20,g-6)
    c: PointOnObject(g19,g-2)
    c: Coincident(g21,g22)
    c: Coincident(g22,g23)
    c: Coincident(g23,g24)
    c: Coincident(g24,g25)
    c: Coincident(g25,g26)
    c: Coincident(g26,g21)
    c: Equal(g21, g22-g26) x5
    c: PointOnObject(g21,g27)
    c: PointOnObject(g22,g27)
    c: PointOnObject(g23,g27)
    c: PointOnObject(g24,g27)
    c: PointOnObject(g25,g27)
    c: PointOnObject(g26,g27)
    c: Radius(g27) = 3
    c: Coincident(g27,g-4)
FEATURE [PartDesign::Pocket] Pocket002
  BaseFeature = -> Chamfer
  Direction = (0,0,-1)
  Length = 2.5
  Length2 = 5
  Profile = -> Sketch004
  ReferenceAxis = -> Sketch004 [N_Axis]
  Refine = true
  Suppressed = false
  Type = 0
FEATURE [PartDesign::Chamfer] Chamfer001
  Angle = 45
  Base = -> Pocket002 [Edge901,Edge900,Edge905,Edge904,Edge903,Edge902,Edge913,Edge912,Edge917,Edge916,Edge915,Edge914,Edge895,Edge894,Edge899,Edge898,Edge897,Edge896,Edge907,Edge906,Edge911,Edge910,Edge909,Edge908]
  BaseFeature = -> Pocket002
  ChamferType = 0
  FlipDirection = false
  Refine = true
  Size = 0.5
  Size2 = 1
  SupportTransform = false
  Suppressed = false
  UseAllEdges = false
FEATURE [PartDesign::Chamfer] Chamfer002
  Angle = 45
  Base = -> Chamfer001 [Edge134,Edge147,Edge148,Edge149]
  BaseFeature = -> Chamfer001
  ChamferType = 0
  FlipDirection = false
  Refine = true
  Size = 0.5
  Size2 = 1
  SupportTransform = false
  Suppressed = false
  UseAllEdges = false
FEATURE [Sketcher::SketchObject] Sketch005
  ArcFitTolerance = 1e-06
  AttachmentSupport = -> [Chamfer002]
  ExternalGeometry = -> [Chamfer002]
  FullyConstrained = true
  MakeInternals = false
  MapMode = 5
  Placement = pos=(0,0,10) rot=(0,0,1;0rad)
  sketch-geometry (1):
    g0: Circle CenterX=0 CenterY=0 CenterZ=0 NormalX=0 NormalY=0 NormalZ=1 AngleXU=0 Radius=5.2
  constraints (2):
    c: Diameter(g0) = 10.4
    c: Coincident(g0,g-1)
FEATURE [PartDesign::Pocket] Pocket003
  BaseFeature = -> Chamfer002
  Direction = (0,0,-1)
  Length = 4.2
  Length2 = 5
  Profile = -> Sketch005
  ReferenceAxis = -> Sketch005 [N_Axis]
  Refine = true
  Suppressed = false
  Type = 0
FEATURE [PartDesign::Chamfer] Chamfer003
  Angle = 45
  Base = -> Pocket003 [Edge45]
  BaseFeature = -> Pocket003
  ChamferType = 0
  FlipDirection = false
  Refine = true
  Size = 0.5
  Size2 = 1
  SupportTransform = false
  Suppressed = false
  UseAllEdges = false
FEATURE [PartDesign::Chamfer] Chamfer004
  Angle = 45
  Base = -> Chamfer003 [Edge131,Edge139]
  BaseFeature = -> Chamfer003
  ChamferType = 0
  FlipDirection = false
  Refine = true
  Size = 0.5
  Size2 = 1
  SupportTransform = false
  Suppressed = false
  UseAllEdges = false
FEATURE [PartDesign::Body] Body
  AllowCompound = false
  BaseFeature = -> TimingGear
  Group = -> [BaseFeature,Sketch,Pad,Sketch001,Sketch002,Pad001,Pocket,Sketch003,Pocket001,Chamfer,Sketch004,Pocket002,Chamfer001,Chamfer002,Sketch005,Pocket003,Chamfer003,Chamfer004]
  Origin = -> Origin
  Tip = -> Chamfer004
---- part pulleys/gt2_48T_pulley_double.FCStd = doc fcstd_6ef7e6a60fe6 ----
FCSTD DOCUMENT  (FreeCAD 1.0R39109 (Git))
Label: gt2_48T_pulley_double
License: All rights reserved
LicenseURL: https://en.wikipedia.org/wiki/All_rights_reserved
objects: Sketcher::SketchObject×8, PartDesign::Pocket×5, PartDesign::Pad×3, PartDesign::Chamfer×2, Part::FeaturePython×1, PartDesign::FeatureBase×1, PartDesign::Mirrored×1, PartDesign::Body×1
note: 52 computed .brp shape members not serialized (recipe doc carries the construction recipe); baked Part::Feature solids carry a one-line shape summary decoded from their .brp

FEATURE [Part::FeaturePython] TimingGear  # WARN: FeaturePython — macro-defined, semantics opaque (R4)
  AttacherType = Attacher::AttachEngine3D
  h = 0.75
  height = 8
  num_teeth = 48
  offset = 0.4
  pitch = 2
  r0 = 0.555
  r1 = 1
  rs = 0.15
  type = 0
  u = 0.254
  version = 1.3.0
FEATURE [PartDesign::FeatureBase] BaseFeature
  BaseFeature = -> TimingGear
  Suppressed = false
FEATURE [Sketcher::SketchObject] Sketch
  ArcFitTolerance = 1e-06
  AttachmentSupport = -> [BaseFeature]
  FullyConstrained = true
  MakeInternals = false
  MapMode = 5
  Placement = pos=(0,0,0) rot=(1,0,0;3.14159rad)
  sketch-geometry (1):
    g0: Circle CenterX=0 CenterY=0 CenterZ=0 NormalX=0 NormalY=0 NormalZ=1 AngleXU=0 Radius=19
  constraints (2):
    c: Diameter(g0) = 38
    c: Coincident(g0,g-1)
FEATURE [PartDesign::Pad] Pad
  BaseFeature = -> BaseFeature
  Direction = (0,0,-1)
  Length = 1
  Length2 = 10
  Profile = -> Sketch
  ReferenceAxis = -> Sketch [N_Axis]
  Refine = true
  Suppressed = false
  Type = 0
FEATURE [Sketcher::SketchObject] Sketch001
  ArcFitTolerance = 1e-06
  AttachmentSupport = -> [Pad]
  FullyConstrained = false
  MakeInternals = false
  MapMode = 5
  Placement = pos=(0,0,-1) rot=(1,0,0;3.14159rad)
  sketch-geometry (6):
    g0: Circle [constr] CenterX=0 CenterY=0 CenterZ=0 NormalX=0 NormalY=0 NormalZ=1 AngleXU=0 Radius=11
    g1: LineSegment [constr] StartX=0 StartY=0 StartZ=0 EndX=0 EndY=11 EndZ=0
    g2: Circle CenterX=0 CenterY=11 CenterZ=0 NormalX=0 NormalY=0 NormalZ=1 AngleXU=0 Radius=1.25
    g3: Circle CenterX=-11 CenterY=0 CenterZ=0 NormalX=0 NormalY=0 NormalZ=1 AngleXU=0 Radius=1.25
    g4: Circle CenterX=0 CenterY=-11 CenterZ=0 NormalX=0 NormalY=0 NormalZ=1 AngleXU=0 Radius=1.25
    g5: Circle CenterX=11 CenterY=0 CenterZ=0 NormalX=0 NormalY=0 NormalZ=1 AngleXU=0 Radius=1.25
  constraints (10):
    c: Diameter(g0) = 22
    c: Coincident(g0,g-1)
    c: Coincident(g1,g0)
    c: PointOnObject(g1,g0)
    c: Vertical(g1)
    c: Coincident(g2,g1)
    c: Diameter(g2) = 2.5
    c: Diameter(g3) = 2.5
    c: Diameter(g4) = 2.5
    c: Diameter(g5) = 2.5
FEATURE [Sketcher::SketchObject] Sketch002
  ArcFitTolerance = 1e-06
  AttachmentSupport = -> [Pad]
  ExternalGeometry = -> [Pad]
  FullyConstrained = true
  MakeInternals = false
  MapMode = 5
  Placement = pos=(0,0,8) rot=(0,0,1;0rad)
  sketch-geometry (1):
    g0: Circle CenterX=0 CenterY=0 CenterZ=0 NormalX=0 NormalY=0 NormalZ=1 AngleXU=0 Radius=19
  constraints (2):
    c: Coincident(g0,g-1)
    c: Diameter(g0) = 38
FEATURE [PartDesign::Pad] Pad001
  BaseFeature = -> Pad
  Direction = (0,0,1)
  Length = 2
  Length2 = 10
  Profile = -> Sketch002
  ReferenceAxis = -> Sketch002 [N_Axis]
  Refine = true
  Suppressed = false
  Type = 0
FEATURE [PartDesign::Pocket] Pocket
  BaseFeature = -> Pad001
  Direction = (0,0,1)
  Length = 29
  Length2 = 5
  Profile = -> Sketch001
  ReferenceAxis = -> Sketch001 [N_Axis]
  Refine = true
  Suppressed = false
  Type = 0
FEATURE [Sketcher::SketchObject] Sketch003
  ArcFitTolerance = 1e-06
  AttachmentSupport = -> [Pocket]
  FullyConstrained = true
  MakeInternals = false
  MapMode = 5
  Placement = pos=(0,0,-1) rot=(1,0,0;3.14159rad)
  sketch-geometry (1):
    g0: Circle CenterX=0 CenterY=0 CenterZ=0 NormalX=0 NormalY=0 NormalZ=1 AngleXU=0 Radius=5
  constraints (2):
    c: Diameter(g0) = 10
    c: Coincident(g0,g-1)
FEATURE [PartDesign::Pocket] Pocket001
  BaseFeature = -> Pocket
  Direction = (0,0,1)
  Length = 17
  Length2 = 5
  Profile = -> Sketch003
  ReferenceAxis = -> Sketch003 [N_Axis]
  Refine = true
  Suppressed = false
  Type = 0
FEATURE [PartDesign::Chamfer] Chamfer
  Angle = 45
  Base = -> Pocket001 [Edge870,Edge297,Edge11,Edge878,Edge879,Edge876,Edge877,Edge880]
  BaseFeature = -> Pocket001
  ChamferType = 0
  FlipDirection = false
  Refine = true
  Size = 0.5
  Size2 = 1
  SupportTransform = false
  Suppressed = false
  UseAllEdges = false
FEATURE [PartDesign::Mirrored] Mirrored
  BaseFeature = -> Chamfer
  MirrorPlane = -> Chamfer [Face293]
  Refine = true
  Suppressed = false
  TransformMode = 1
FEATURE [Sketcher::SketchObject] Sketch004
  ArcFitTolerance = 1e-06
  AttachmentSupport = -> [Mirrored]
  ExternalGeometry = -> [Mirrored]
  FullyConstrained = false
  MakeInternals = false
  MapMode = 5
  Placement = pos=(0,0,-12) rot=(1,0,0;3.14159rad)
  sketch-geometry (5):
    g0: Circle CenterX=0 CenterY=0 CenterZ=0 NormalX=0 NormalY=0 NormalZ=1 AngleXU=0 Radius=7.1969
    g1: Circle CenterX=0 CenterY=11 CenterZ=0 NormalX=0 NormalY=0 NormalZ=1 AngleXU=0 Radius=2.72357
    g2: Circle CenterX=-11 CenterY=0 CenterZ=0 NormalX=0 NormalY=0 NormalZ=1 AngleXU=0 Radius=2.65153
    g3: Circle CenterX=0 CenterY=-11 CenterZ=0 NormalX=0 NormalY=0 NormalZ=1 AngleXU=0 Radius=3.2579
    g4: Circle CenterX=11 CenterY=0 CenterZ=0 NormalX=0 NormalY=0 NormalZ=1 AngleXU=0 Radius=3.02055
  constraints (5):
    c: Coincident(g0,g-1)
    c: Coincident(g1,g-3)
    c: Coincident(g2,g-4)
    c: Coincident(g3,g-5)
    c: Coincident(g4,g-6)
FEATURE [PartDesign::Pad] Pad002
  BaseFeature = -> Mirrored
  Direction = (0,0,-1)
  Length = 22
  Length2 = 10
  Profile = -> Sketch004
  ReferenceAxis = -> Sketch004 [N_Axis]
  Refine = true
  Reversed = true
  Suppressed = false
  Type = 0
FEATURE [Sketcher::SketchObject] Sketch005
  ArcFitTolerance = 1e-06
  AttachmentSupport = -> [Pad002]
  FullyConstrained = true
  MakeInternals = false
  MapMode = 5
  Placement = pos=(0,0,-12) rot=(1,0,0;3.14159rad)
  sketch-geometry (1):
    g0: Circle CenterX=0 CenterY=0 CenterZ=0 NormalX=0 NormalY=0 NormalZ=1 AngleXU=0 Radius=3
  constraints (2):
    c: Coincident(g0,g-1)
    c: Diameter(g0) = 6
FEATURE [PartDesign::Pocket] Pocket002
  BaseFeature = -> Pad002
  Direction = (0,0,1)
  Length = 5
  Length2 = 5
  Profile = -> Sketch005
  ReferenceAxis = -> Sketch005 [N_Axis]
  Refine = true
  Suppressed = false
  Type = 1
FEATURE [Sketcher::SketchObject] Sketch006
  ArcFitTolerance = 1e-06
  AttachmentSupport = -> [Pocket002]
  FullyConstrained = true
  MakeInternals = false
  MapMode = 5
  Placement = pos=(0,0,-12) rot=(1,0,0;3.14159rad)
  sketch-geometry (1):
    g0: Circle CenterX=0 CenterY=0 CenterZ=0 NormalX=0 NormalY=0 NormalZ=1 AngleXU=0 Radius=5.2
  constraints (2):
    c: Coincident(g0,g-1)
    c: Diameter(g0) = 10.4
FEATURE [PartDesign::Pocket] Pocket003
  BaseFeature = -> Pocket002
  Direction = (0,0,1)
  Length = 4
  Length2 = 5
  Profile = -> Sketch006
  ReferenceAxis = -> Sketch006 [N_Axis]
  Refine = true
  Suppressed = false
  Type = 0
FEATURE [Sketcher::SketchObject] Sketch007
  ArcFitTolerance = 1e-06
  AttachmentSupport = -> [Pocket003]
  FullyConstrained = true
  MakeInternals = false
  MapMode = 5
  Placement = pos=(0,0,10) rot=(0,0,1;0rad)
  sketch-geometry (1):
    g0: Circle CenterX=0 CenterY=0 CenterZ=0 NormalX=0 NormalY=0 NormalZ=1 AngleXU=0 Radius=5.2
  constraints (2):
    c: Coincident(g0,g-1)
    c: Diameter(g0) = 10.4
FEATURE [PartDesign::Pocket] Pocket004
  BaseFeature = -> Pocket003
  Direction = (0,0,-1)
  Length = 4
  Length2 = 5
  Profile = -> Sketch007
  ReferenceAxis = -> Sketch007 [N_Axis]
  Refine = true
  Suppressed = false
  Type = 0
FEATURE [PartDesign::Chamfer] Chamfer001
  Angle = 45
  Base = -> Pocket004 [Edge1754,Edge1746]
  BaseFeature = -> Pocket004
  ChamferType = 0
  FlipDirection = false
  Refine = true
  Size = 0.5
  Size2 = 1
  SupportTransform = false
  Suppressed = false
  UseAllEdges = false
FEATURE [PartDesign::Body] Body
  AllowCompound = false
  BaseFeature = -> TimingGear
  Group = -> [BaseFeature,Sketch,Pad,Sketch001,Sketch002,Pad001,Pocket,Sketch003,Pocket001,Chamfer,Mirrored,Sketch004,Pad002,Sketch005,Pocket002,Sketch006,Pocket003,Sketch007,Pocket004,Chamfer001]
  Origin = -> Origin
  Tip = -> Chamfer001
